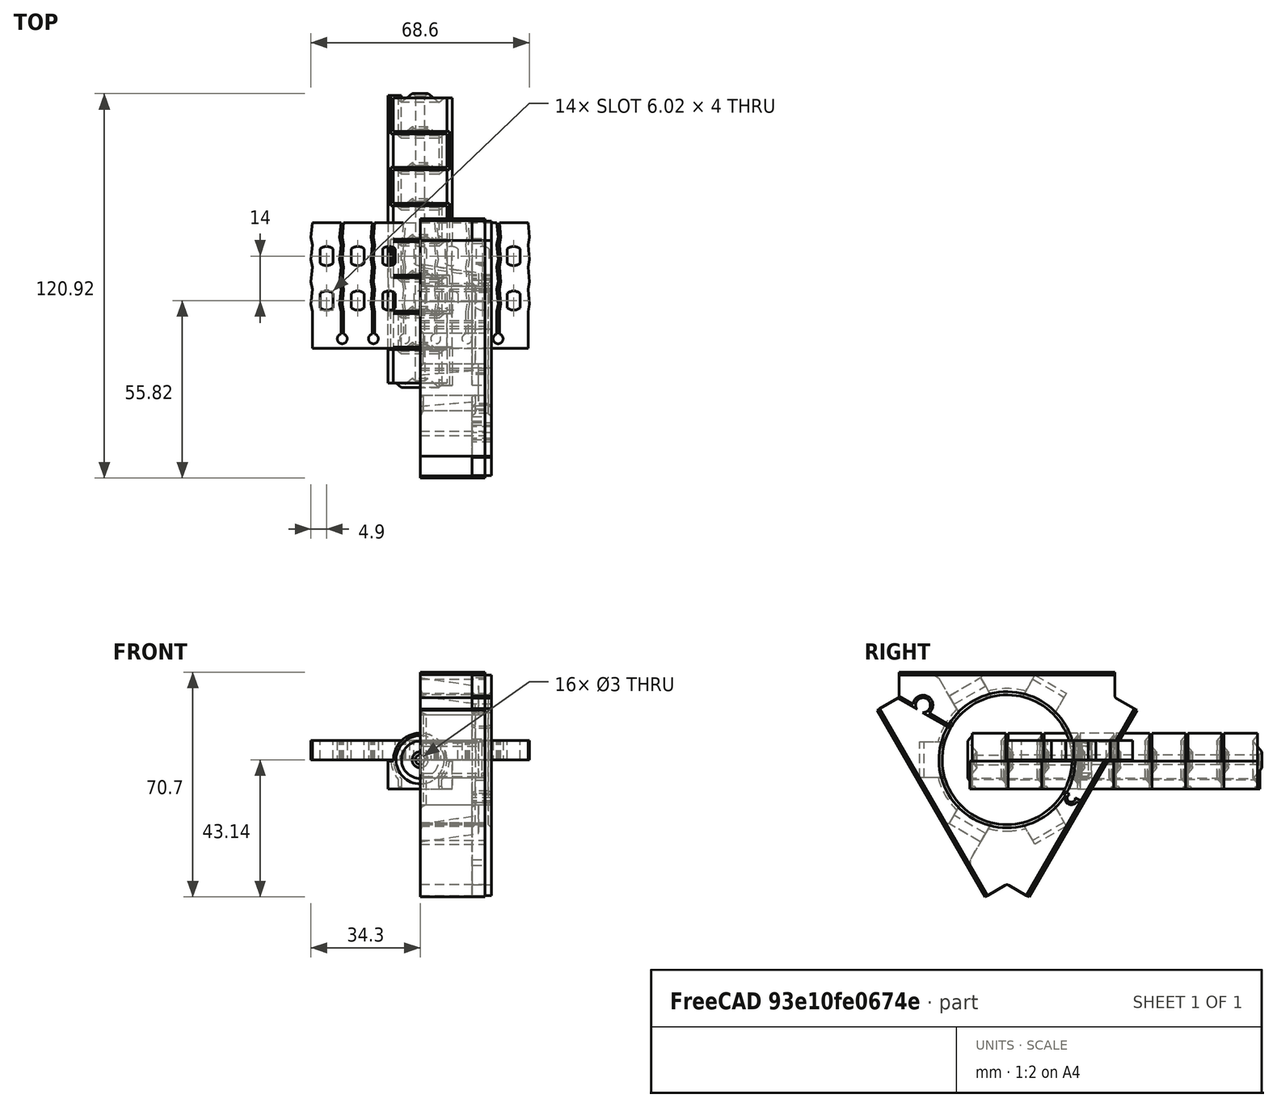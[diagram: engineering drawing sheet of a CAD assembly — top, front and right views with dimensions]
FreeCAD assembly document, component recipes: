
FREECAD ASSEMBLY — COMPONENT RECIPES ("BaseHingeModel_ver1.2_Transmission")

This assembly document has 7 components, labeled P0..P6 below (a component is one placed body or linked part). 6 of them carry a construction recipe — the FreeCAD feature program that regenerates the part from scratch, quoted from this document or its linked companion documents; the rest are supplied as boundary geometry only. No exploded tour is included for this assembly.
COMPONENT P0 — geometry summary ("Assembly"; no construction recipe available for this part):
  bounding box: 182.8 x 158.8 x 20.4 mm
  tessellated surface: 20,696 triangles
  volume: 9578097130411803656351970426578674498653964242418576373807381627235447409514995756881183408189511817567906541525464308833607482709359269325981809199022080 mm^3 (1616738801575943140395693637715189882977871249383409942478852649766611869419882643060896964713126329768861879254438412431142423713072396559864123359232% of its bounding box)
COMPONENT P1 — recipe-attached ("BeamFixatoPart", modeled in this document).
Construction recipe (the document's own serialized feature program — sketch geometry with constraints, then the solid features built on it; lengths are millimeters unless a unit is written):

FEATURE [Sketcher::SketchObject] Sketch022  label="FixatorBodySketch"
  FullyConstrained = false
  MapMode = 5
  Support = -> [XY_Plane005]
  expr: Constraints[143] = Spreadsheet.mmCellWall
  expr: Constraints[144] = Spreadsheet.mmCellWall
  expr: Constraints[145] = Spreadsheet.mmCellWall
  expr: Constraints[146] = Spreadsheet.mmCellWidth
  expr: Constraints[147] = Spreadsheet.mmCellWidth
  expr: Constraints[148] = Spreadsheet.mmCellWidth
  expr: Constraints[169] = Spreadsheet.mmCommonBaseLenght
  expr: Constraints[170] = Spreadsheet.mmToothStep
  expr: Constraints[171] = Spreadsheet.mmToothStep
  expr: Constraints[172] = Spreadsheet.mmToothStep
  expr: Constraints[173] = Spreadsheet.mmToothStep
  expr: Constraints[174] = Spreadsheet.mmToothStep
  expr: Constraints[183] = Spreadsheet.mmCellWall * 3
  expr: Constraints[184] = Spreadsheet.mmCellWall * 3
  expr: Constraints[185] = Spreadsheet.mmCellWall * 3
  expr: Constraints[186] = Spreadsheet.mmCellWall * 3
  expr: Constraints[425] = Spreadsheet.mmFirstCircleArcToBase
  expr: Constraints[435] = Spreadsheet.mmCellWall / 2
  expr: Constraints[464] = Spreadsheet.mmCellWidth + Spreadsheet.mmCellWall
  expr: Constraints[5] = Spreadsheet.mmBaseWidth
  expr: Constraints[6] = Spreadsheet.mmBaseEnd
  sketch-geometry (155):
    g0: LineSegment StartX=-33.9 StartY=0 StartZ=0 EndX=-33.9 EndY=39.5 EndZ=0
    g1: LineSegment StartX=-33.9 StartY=39.5 StartZ=0 EndX=33.9 EndY=39.5 EndZ=0
    g2: LineSegment StartX=33.9 StartY=39.5 StartZ=0 EndX=33.9 EndY=0 EndZ=0
    g3: LineSegment StartX=-73.1099 StartY=25.5 StartZ=0 EndX=65.6354 EndY=25.5 EndZ=0
    g4: LineSegment StartX=-33.9 StartY=0 StartZ=0 EndX=-33.9 EndY=11.5 EndZ=0
    g5: LineSegment StartX=-33.9 StartY=11.5 StartZ=0 EndX=-34.3 EndY=13.9 EndZ=0
    g6: LineSegment StartX=-34.3 StartY=13.9 StartZ=0 EndX=-33.9 EndY=18.5 EndZ=0
    g7: LineSegment StartX=-33.9 StartY=18.5 StartZ=0 EndX=-34.3 EndY=20.9 EndZ=0
    g8: LineSegment StartX=-34.3 StartY=20.9 StartZ=0 EndX=-33.9 EndY=25.5 EndZ=0
    g9: LineSegment StartX=-33.9 StartY=25.5 StartZ=0 EndX=-34.3 EndY=27.9 EndZ=0
    g10: LineSegment StartX=-34.3 StartY=27.9 StartZ=0 EndX=-33.9 EndY=32.5 EndZ=0
    g11: LineSegment StartX=-33.9 StartY=32.5 StartZ=0 EndX=-34.3 EndY=34.9 EndZ=0
    g12: LineSegment StartX=-34.3 StartY=34.9 StartZ=0 EndX=-33.9 EndY=39.5 EndZ=0
    g13: LineSegment StartX=-33.9 StartY=39.5 StartZ=0 EndX=-24.9 EndY=39.5 EndZ=0
    g14: LineSegment StartX=-24.9 StartY=39.5 StartZ=0 EndX=-25.3 EndY=34.9 EndZ=0
    g15: LineSegment StartX=-25.3 StartY=34.9 StartZ=0 EndX=-24.9 EndY=32.5 EndZ=0
    g16: LineSegment StartX=-24.9 StartY=32.5 StartZ=0 EndX=-25.3 EndY=27.9 EndZ=0
    g17: LineSegment StartX=-25.3 StartY=27.9 StartZ=0 EndX=-24.9 EndY=25.5 EndZ=0
    g18: LineSegment StartX=-24.9 StartY=25.5 StartZ=0 EndX=-25.3 EndY=20.9 EndZ=0
    g19: LineSegment StartX=-25.3 StartY=20.9 StartZ=0 EndX=-24.9 EndY=18.5 EndZ=0
    g20: LineSegment StartX=-24.9 StartY=18.5 StartZ=0 EndX=-25.3 EndY=13.9 EndZ=0
    g21: LineSegment StartX=-25.3 StartY=13.9 StartZ=0 EndX=-24.9 EndY=11.5 EndZ=0
    g22: LineSegment StartX=-24.9 StartY=11.5 StartZ=0 EndX=-24.9 EndY=4.5 EndZ=0
    g23: LineSegment StartX=-24.1 StartY=4.5 StartZ=0 EndX=-24.1 EndY=11.5 EndZ=0
    g24: LineSegment StartX=-24.1 StartY=11.5 StartZ=0 EndX=-24.5 EndY=13.9 EndZ=0
    g25: LineSegment StartX=-24.5 StartY=13.9 StartZ=0 EndX=-24.1 EndY=18.5 EndZ=0
    g26: LineSegment StartX=-24.1 StartY=18.5 StartZ=0 EndX=-24.5 EndY=20.9 EndZ=0
    g27: LineSegment StartX=-24.5 StartY=20.9 StartZ=0 EndX=-24.1 EndY=25.5 EndZ=0
    g28: LineSegment StartX=-24.1 StartY=25.5 StartZ=0 EndX=-24.5 EndY=27.9 EndZ=0
    g29: LineSegment StartX=-24.5 StartY=27.9 StartZ=0 EndX=-24.1 EndY=32.5 EndZ=0
    g30: LineSegment StartX=-24.1 StartY=32.5 StartZ=0 EndX=-24.5 EndY=34.9 EndZ=0
    g31: LineSegment StartX=-24.5 StartY=34.9 StartZ=0 EndX=-24.1 EndY=39.5 EndZ=0
    g32: LineSegment StartX=-24.1 StartY=39.5 StartZ=0 EndX=-15.1 EndY=39.5 EndZ=0
    g33: LineSegment StartX=-15.1 StartY=39.5 StartZ=0 EndX=-15.5 EndY=34.9 EndZ=0
    g34: LineSegment StartX=-15.5 StartY=34.9 StartZ=0 EndX=-15.1 EndY=32.5 EndZ=0
    g35: LineSegment StartX=-15.1 StartY=32.5 StartZ=0 EndX=-15.5 EndY=27.9 EndZ=0
    g36: LineSegment StartX=-15.5 StartY=27.9 StartZ=0 EndX=-15.1 EndY=25.5 EndZ=0
    g37: LineSegment StartX=-15.1 StartY=25.5 StartZ=0 EndX=-15.5 EndY=20.9 EndZ=0
    g38: LineSegment StartX=-15.5 StartY=20.9 StartZ=0 EndX=-15.1 EndY=18.5 EndZ=0
    g39: LineSegment StartX=-15.1 StartY=18.5 StartZ=0 EndX=-15.5 EndY=13.9 EndZ=0
    g40: LineSegment StartX=-15.5 StartY=13.9 StartZ=0 EndX=-15.1 EndY=11.5 EndZ=0
    g41: LineSegment StartX=-15.1 StartY=11.5 StartZ=0 EndX=-15.1 EndY=4.5 EndZ=0
    g42: LineSegment StartX=-14.3 StartY=4.5 StartZ=0 EndX=-14.3 EndY=11.5 EndZ=0
    g43: LineSegment StartX=-14.3 StartY=11.5 StartZ=0 EndX=-14.7 EndY=13.9 EndZ=0
    g44: LineSegment StartX=-14.7 StartY=13.9 StartZ=0 EndX=-14.3 EndY=18.5 EndZ=0
    g45: LineSegment StartX=-14.3 StartY=18.5 StartZ=0 EndX=-14.7 EndY=20.9 EndZ=0
    g46: LineSegment StartX=-14.7 StartY=20.9 StartZ=0 EndX=-14.3 EndY=25.5 EndZ=0
    g47: LineSegment StartX=-14.3 StartY=25.5 StartZ=0 EndX=-14.7 EndY=27.9 EndZ=0
    g48: LineSegment StartX=-14.7 StartY=27.9 StartZ=0 EndX=-14.3 EndY=32.5 EndZ=0
    g49: LineSegment StartX=-14.3 StartY=32.5 StartZ=0 EndX=-14.7 EndY=34.9 EndZ=0
    g50: LineSegment StartX=-14.7 StartY=34.9 StartZ=0 EndX=-14.3 EndY=39.5 EndZ=0
    g51: LineSegment StartX=-14.3 StartY=39.5 StartZ=0 EndX=-5.3 EndY=39.5 EndZ=0
    g52: LineSegment StartX=-5.3 StartY=39.5 StartZ=0 EndX=-5.7 EndY=34.9 EndZ=0
    g53: LineSegment StartX=-5.7 StartY=34.9 StartZ=0 EndX=-5.3 EndY=32.5 EndZ=0
    g54: LineSegment StartX=-5.3 StartY=32.5 StartZ=0 EndX=-5.7 EndY=27.9 EndZ=0
    g55: LineSegment StartX=-5.7 StartY=27.9 StartZ=0 EndX=-5.3 EndY=25.5 EndZ=0
    g56: LineSegment StartX=-5.3 StartY=25.5 StartZ=0 EndX=-5.7 EndY=20.9 EndZ=0
    g57: LineSegment StartX=-5.7 StartY=20.9 StartZ=0 EndX=-5.3 EndY=18.5 EndZ=0
    g58: LineSegment StartX=-5.3 StartY=18.5 StartZ=0 EndX=-5.7 EndY=13.9 EndZ=0
    g59: LineSegment StartX=-5.7 StartY=13.9 StartZ=0 EndX=-5.3 EndY=11.5 EndZ=0
    g60: LineSegment StartX=-5.3 StartY=11.5 StartZ=0 EndX=-5.3 EndY=4.5 EndZ=0
    g61: LineSegment StartX=-4.5 StartY=4.5 StartZ=0 EndX=-4.5 EndY=11.5 EndZ=0
    g62: LineSegment StartX=-4.5 StartY=11.5 StartZ=0 EndX=-4.9 EndY=13.9 EndZ=0
    g63: LineSegment StartX=-4.9 StartY=13.9 StartZ=0 EndX=-4.5 EndY=18.5 EndZ=0
    g64: LineSegment StartX=-4.5 StartY=18.5 StartZ=0 EndX=-4.9 EndY=20.9 EndZ=0
    g65: LineSegment StartX=-4.9 StartY=20.9 StartZ=0 EndX=-4.5 EndY=25.5 EndZ=0
    g66: LineSegment StartX=-4.5 StartY=25.5 StartZ=0 EndX=-4.9 EndY=27.9 EndZ=0
    g67: LineSegment StartX=-4.9 StartY=27.9 StartZ=0 EndX=-4.5 EndY=32.5 EndZ=0
    g68: LineSegment StartX=-4.5 StartY=32.5 StartZ=0 EndX=-4.9 EndY=34.9 EndZ=0
    g69: LineSegment StartX=-4.9 StartY=34.9 StartZ=0 EndX=-4.5 EndY=39.5 EndZ=0
    g70: LineSegment StartX=-4.5 StartY=39.5 StartZ=0 EndX=4.5 EndY=39.5 EndZ=0
    g71: LineSegment StartX=4.5 StartY=39.5 StartZ=0 EndX=4.9 EndY=34.9 EndZ=0
    g72: LineSegment StartX=4.9 StartY=34.9 StartZ=0 EndX=4.5 EndY=32.5 EndZ=0
    g73: LineSegment StartX=4.5 StartY=32.5 StartZ=0 EndX=4.9 EndY=27.9 EndZ=0
    g74: LineSegment StartX=4.9 StartY=27.9 StartZ=0 EndX=4.5 EndY=25.5 EndZ=0
    g75: LineSegment StartX=4.5 StartY=25.5 StartZ=0 EndX=4.9 EndY=20.9 EndZ=0
    g76: LineSegment StartX=4.9 StartY=20.9 StartZ=0 EndX=4.5 EndY=18.5 EndZ=0
    g77: LineSegment StartX=4.5 StartY=18.5 StartZ=0 EndX=4.9 EndY=13.9 EndZ=0
    g78: LineSegment StartX=4.9 StartY=13.9 StartZ=0 EndX=4.5 EndY=11.5 EndZ=0
    g79: LineSegment StartX=4.5 StartY=11.5 StartZ=0 EndX=4.5 EndY=4.5 EndZ=0
    g80: LineSegment StartX=5.3 StartY=4.5 StartZ=0 EndX=5.3 EndY=11.5 EndZ=0
    g81: LineSegment StartX=5.3 StartY=11.5 StartZ=0 EndX=5.7 EndY=13.9 EndZ=0
    g82: LineSegment StartX=5.7 StartY=13.9 StartZ=0 EndX=5.3 EndY=18.5 EndZ=0
    g83: LineSegment StartX=5.3 StartY=18.5 StartZ=0 EndX=5.7 EndY=20.9 EndZ=0
    g84: LineSegment StartX=5.7 StartY=20.9 StartZ=0 EndX=5.3 EndY=25.5 EndZ=0
    g85: LineSegment StartX=5.3 StartY=25.5 StartZ=0 EndX=5.7 EndY=27.9 EndZ=0
    g86: LineSegment StartX=5.7 StartY=27.9 StartZ=0 EndX=5.3 EndY=32.5 EndZ=0
    g87: LineSegment StartX=5.3 StartY=32.5 StartZ=0 EndX=5.7 EndY=34.9 EndZ=0
    g88: LineSegment StartX=5.7 StartY=34.9 StartZ=0 EndX=5.3 EndY=39.5 EndZ=0
    g89: LineSegment StartX=5.3 StartY=39.5 StartZ=0 EndX=14.3 EndY=39.5 EndZ=0
    g90: LineSegment StartX=14.3 StartY=39.5 StartZ=0 EndX=14.7 EndY=34.9 EndZ=0
    g91: LineSegment StartX=14.7 StartY=34.9 StartZ=0 EndX=14.3 EndY=32.5 EndZ=0
    g92: LineSegment StartX=14.3 StartY=32.5 StartZ=0 EndX=14.7 EndY=27.9 EndZ=0
    g93: LineSegment StartX=14.7 StartY=27.9 StartZ=0 EndX=14.3 EndY=25.5 EndZ=0
    g94: LineSegment StartX=14.3 StartY=25.5 StartZ=0 EndX=14.7 EndY=20.9 EndZ=0
    g95: LineSegment StartX=14.7 StartY=20.9 StartZ=0 EndX=14.3 EndY=18.5 EndZ=0
    g96: LineSegment StartX=14.3 StartY=18.5 StartZ=0 EndX=14.7 EndY=13.9 EndZ=0
    g97: LineSegment StartX=14.7 StartY=13.9 StartZ=0 EndX=14.3 EndY=11.5 EndZ=0
    g98: LineSegment StartX=14.3 StartY=11.5 StartZ=0 EndX=14.3 EndY=4.5 EndZ=0
    g99: LineSegment StartX=15.1 StartY=4.5 StartZ=0 EndX=15.1 EndY=11.5 EndZ=0
    g100: LineSegment StartX=15.1 StartY=11.5 StartZ=0 EndX=15.5 EndY=13.9 EndZ=0
    g101: LineSegment StartX=15.5 StartY=13.9 StartZ=0 EndX=15.1 EndY=18.5 EndZ=0
    g102: LineSegment StartX=15.1 StartY=18.5 StartZ=0 EndX=15.5 EndY=20.9 EndZ=0
    g103: LineSegment StartX=15.5 StartY=20.9 StartZ=0 EndX=15.1 EndY=25.5 EndZ=0
    g104: LineSegment StartX=15.1 StartY=25.5 StartZ=0 EndX=15.5 EndY=27.9 EndZ=0
    g105: LineSegment StartX=15.5 StartY=27.9 StartZ=0 EndX=15.1 EndY=32.5 EndZ=0
    g106: LineSegment StartX=15.1 StartY=32.5 StartZ=0 EndX=15.5 EndY=34.9 EndZ=0
    g107: LineSegment StartX=15.5 StartY=34.9 StartZ=0 EndX=15.1 EndY=39.5 EndZ=0
    g108: LineSegment StartX=15.1 StartY=39.5 StartZ=0 EndX=24.1 EndY=39.5 EndZ=0
    g109: LineSegment StartX=24.1 StartY=39.5 StartZ=0 EndX=24.5 EndY=34.9 EndZ=0
    g110: LineSegment StartX=24.5 StartY=34.9 StartZ=0 EndX=24.1 EndY=32.5 EndZ=0
    g111: LineSegment StartX=24.1 StartY=32.5 StartZ=0 EndX=24.5 EndY=27.9 EndZ=0
    g112: LineSegment StartX=24.5 StartY=27.9 StartZ=0 EndX=24.1 EndY=25.5 EndZ=0
    g113: LineSegment StartX=24.1 StartY=25.5 StartZ=0 EndX=24.5 EndY=20.9 EndZ=0
    g114: LineSegment StartX=24.5 StartY=20.9 StartZ=0 EndX=24.1 EndY=18.5 EndZ=0
    g115: LineSegment StartX=24.1 StartY=18.5 StartZ=0 EndX=24.5 EndY=13.9 EndZ=0
    g116: LineSegment StartX=24.5 StartY=13.9 StartZ=0 EndX=24.1 EndY=11.5 EndZ=0
    g117: LineSegment StartX=24.1 StartY=11.5 StartZ=0 EndX=24.1 EndY=4.5 EndZ=0
    g118: LineSegment StartX=24.9 StartY=4.5 StartZ=0 EndX=24.9 EndY=11.5 EndZ=0
    g119: LineSegment StartX=24.9 StartY=11.5 StartZ=0 EndX=25.3 EndY=13.9 EndZ=0
    g120: LineSegment StartX=25.3 StartY=13.9 StartZ=0 EndX=24.9 EndY=18.5 EndZ=0
    g121: LineSegment StartX=24.9 StartY=18.5 StartZ=0 EndX=25.3 EndY=20.9 EndZ=0
    g122: LineSegment StartX=25.3 StartY=20.9 StartZ=0 EndX=24.9 EndY=25.5 EndZ=0
    g123: LineSegment StartX=24.9 StartY=25.5 StartZ=0 EndX=25.3 EndY=27.9 EndZ=0
    g124: LineSegment StartX=25.3 StartY=27.9 StartZ=0 EndX=24.9 EndY=32.5 EndZ=0
    g125: LineSegment StartX=24.9 StartY=32.5 StartZ=0 EndX=25.3 EndY=34.9 EndZ=0
    g126: LineSegment StartX=25.3 StartY=34.9 StartZ=0 EndX=24.9 EndY=39.5 EndZ=0
    g127: LineSegment StartX=24.9 StartY=39.5 StartZ=0 EndX=33.9 EndY=39.5 EndZ=0
    g128: LineSegment StartX=33.9 StartY=39.5 StartZ=0 EndX=34.3 EndY=34.9 EndZ=0
    g129: LineSegment StartX=34.3 StartY=34.9 StartZ=0 EndX=33.9 EndY=32.5 EndZ=0
    g130: LineSegment StartX=33.9 StartY=32.5 StartZ=0 EndX=34.3 EndY=27.9 EndZ=0
    g131: LineSegment StartX=34.3 StartY=27.9 StartZ=0 EndX=33.9 EndY=25.5 EndZ=0
    g132: LineSegment StartX=33.9 StartY=25.5 StartZ=0 EndX=34.3 EndY=20.9 EndZ=0
    g133: LineSegment StartX=34.3 StartY=20.9 StartZ=0 EndX=33.9 EndY=18.5 EndZ=0
    g134: LineSegment StartX=33.9 StartY=18.5 StartZ=0 EndX=34.3 EndY=13.9 EndZ=0
    g135: LineSegment StartX=34.3 StartY=13.9 StartZ=0 EndX=33.9 EndY=11.5 EndZ=0
    g136: LineSegment StartX=33.9 StartY=11.5 StartZ=0 EndX=33.9 EndY=0 EndZ=0
    g137: LineSegment StartX=33.9 StartY=0 StartZ=0 EndX=-33.9 EndY=0 EndZ=0
    g138: LineSegment StartX=-73.1099 StartY=18.5 StartZ=0 EndX=65.6354 EndY=18.5 EndZ=0
    g139: LineSegment StartX=-73.1099 StartY=34.9 StartZ=0 EndX=65.6354 EndY=34.9 EndZ=0
    g140: LineSegment StartX=-73.1099 StartY=32.5 StartZ=0 EndX=65.6354 EndY=32.5 EndZ=0
    g141: LineSegment StartX=-73.1099 StartY=27.9 StartZ=0 EndX=65.6354 EndY=27.9 EndZ=0
    g142: LineSegment StartX=-73.1099 StartY=20.9 StartZ=0 EndX=65.6354 EndY=20.9 EndZ=0
    g143: LineSegment StartX=-73.1099 StartY=11.5 StartZ=0 EndX=65.6354 EndY=11.5 EndZ=0
    g144: LineSegment StartX=-34.3 StartY=8.59208 StartZ=0 EndX=-34.3 EndY=49.4346 EndZ=0
    g145: LineSegment StartX=-73.1099 StartY=13.9 StartZ=0 EndX=65.6354 EndY=13.9 EndZ=0
    g146: LineSegment StartX=-33.9 StartY=0 StartZ=0 EndX=33.9 EndY=0 EndZ=0
    g147: LineSegment StartX=-73.1099 StartY=4.5 StartZ=0 EndX=65.6354 EndY=4.5 EndZ=0
    g148: ArcOfCircle CenterX=-24.5 CenterY=3 CenterZ=0 NormalX=0 NormalY=0 NormalZ=1 AngleXU=0 Radius=1.55242 StartAngle=1.8314 EndAngle=7.59338
    g149: ArcOfCircle CenterX=-14.7 CenterY=3 CenterZ=0 NormalX=0 NormalY=0 NormalZ=1 AngleXU=0 Radius=1.55242 StartAngle=1.8314 EndAngle=7.59338
    g150: ArcOfCircle CenterX=-4.9 CenterY=3 CenterZ=0 NormalX=0 NormalY=0 NormalZ=1 AngleXU=0 Radius=1.55242 StartAngle=1.8314 EndAngle=7.59338
    g151: ArcOfCircle CenterX=4.9 CenterY=3 CenterZ=0 NormalX=0 NormalY=0 NormalZ=1 AngleXU=0 Radius=1.55242 StartAngle=1.8314 EndAngle=7.59338
    g152: ArcOfCircle CenterX=14.7 CenterY=3 CenterZ=0 NormalX=0 NormalY=0 NormalZ=1 AngleXU=0 Radius=1.55242 StartAngle=1.8314 EndAngle=7.59338
    g153: ArcOfCircle CenterX=24.5 CenterY=3 CenterZ=0 NormalX=0 NormalY=0 NormalZ=1 AngleXU=0 Radius=1.55242 StartAngle=1.8314 EndAngle=7.59338
    g154: LineSegment StartX=-73.1099 StartY=3 StartZ=0 EndX=65.6354 EndY=3 EndZ=0
  constraints (469):
    c: Coincident(g0,g1)
    c: Coincident(g1,g2)
    c: Horizontal(g3)
    c: Symmetric(g0,g2,g-2)
    c: Symmetric(g1,g0,g-2)
    c: DistanceX(g0,g2) = 67.8
    c: DistanceX(g0,g1) = 67.8
    c: Coincident(g4,g5)
    c: Coincident(g5,g6)
    c: Coincident(g6,g7)
    c: Coincident(g7,g8)
    c: Coincident(g8,g9)
    c: Coincident(g9,g10)
    c: Coincident(g10,g11)
    c: Coincident(g11,g12)
    c: Coincident(g12,g13)
    c: Horizontal(g13)
    c: Coincident(g13,g14)
    c: Coincident(g14,g15)
    c: Coincident(g15,g16)
    c: Coincident(g16,g17)
    c: Coincident(g17,g18)
    c: Coincident(g18,g19)
    c: Coincident(g19,g20)
    c: Coincident(g20,g21)
    c: Coincident(g21,g22)
    c: Coincident(g23,g24)
    c: Coincident(g24,g25)
    c: Coincident(g25,g26)
    c: Coincident(g26,g27)
    c: Coincident(g27,g28)
    c: Coincident(g28,g29)
    c: Coincident(g29,g30)
    c: Coincident(g30,g31)
    c: Coincident(g31,g32)
    c: Horizontal(g32)
    c: Coincident(g32,g33)
    c: Coincident(g33,g34)
    c: Coincident(g34,g35)
    c: Coincident(g35,g36)
    c: Coincident(g36,g37)
    c: Coincident(g37,g38)
    c: Coincident(g38,g39)
    c: Coincident(g39,g40)
    c: Coincident(g40,g41)
    c: Coincident(g42,g43)
    c: Coincident(g43,g44)
    c: Coincident(g44,g45)
    c: Coincident(g45,g46)
    c: Coincident(g46,g47)
    c: Coincident(g47,g48)
    c: Coincident(g48,g49)
    c: Coincident(g49,g50)
    c: Coincident(g50,g51)
    c: Coincident(g51,g52)
    c: Coincident(g52,g53)
    c: Coincident(g53,g54)
    c: Coincident(g54,g55)
    c: Coincident(g55,g56)
    c: Coincident(g56,g57)
    c: Coincident(g57,g58)
    c: Coincident(g58,g59)
    c: Coincident(g59,g60)
    c: Coincident(g61,g62)
    c: Coincident(g62,g63)
    c: Coincident(g63,g64)
    c: Coincident(g64,g65)
    c: Coincident(g65,g66)
    c: Coincident(g66,g67)
    c: Coincident(g67,g68)
    c: Coincident(g68,g69)
    c: Coincident(g69,g70)
    c: Coincident(g70,g71)
    c: Coincident(g71,g72)
    c: Coincident(g72,g73)
    c: Coincident(g73,g74)
    c: Coincident(g74,g75)
    c: Coincident(g75,g76)
    c: Coincident(g76,g77)
    c: Coincident(g77,g78)
    c: Coincident(g78,g79)
    c: Coincident(g80,g81)
    c: Coincident(g81,g82)
    c: Coincident(g82,g83)
    c: Coincident(g83,g84)
    c: Coincident(g84,g85)
    c: Coincident(g85,g86)
    c: Coincident(g86,g87)
    c: Coincident(g87,g88)
    c: Coincident(g88,g89)
    c: Horizontal(g89)
    c: Coincident(g89,g90)
    c: Coincident(g90,g91)
    c: Coincident(g91,g92)
    c: Coincident(g92,g93)
    c: Coincident(g93,g94)
    c: Coincident(g94,g95)
    c: Coincident(g95,g96)
    c: Coincident(g96,g97)
    c: Coincident(g97,g98)
    c: Coincident(g99,g100)
    c: Coincident(g100,g101)
    c: Coincident(g101,g102)
    c: Coincident(g102,g103)
    c: Coincident(g103,g104)
    c: Coincident(g104,g105)
    c: Coincident(g105,g106)
    c: Coincident(g106,g107)
    c: Coincident(g107,g108)
    c: Coincident(g108,g109)
    c: Coincident(g109,g110)
    c: Coincident(g110,g111)
    c: Coincident(g111,g112)
    c: Coincident(g112,g113)
    c: Coincident(g113,g114)
    c: Coincident(g114,g115)
    c: Coincident(g115,g116)
    c: Coincident(g116,g117)
    c: Coincident(g118,g119)
    c: Coincident(g119,g120)
    c: Coincident(g120,g121)
    c: Coincident(g121,g122)
    c: Coincident(g122,g123)
    c: Coincident(g123,g124)
    c: Coincident(g124,g125)
    c: Coincident(g125,g126)
    c: Coincident(g126,g127)
    c: Coincident(g127,g128)
    c: Coincident(g128,g129)
    c: Coincident(g129,g130)
    c: Coincident(g130,g131)
    c: Coincident(g131,g132)
    c: Coincident(g132,g133)
    c: Coincident(g133,g134)
    c: Coincident(g134,g135)
    c: Coincident(g135,g136)
    c: Symmetric(g69,g70,g-2)
    c: Symmetric(g51,g88,g-2)
    c: Symmetric(g50,g89,g-2)
    c: Symmetric(g32,g107,g-2)
    c: Symmetric(g31,g108,g-2)
    c: Symmetric(g13,g126,g-2)
    c: Symmetric(g12,g127,g-2)
    c: DistanceX(g13,g31) = 0.8
    c: DistanceX(g32,g50) = 0.8
    c: DistanceX(g51,g69) = 0.8
    c: DistanceX(g13,g13) = 9
    c: DistanceX(g32,g32) = 9
    c: DistanceX(g51,g51) = 9
    c: Horizontal(g139)
    c: Horizontal(g140)
    c: Horizontal(g141)
    c: Horizontal(g142)
    c: Horizontal(g143)
    c: Vertical(g8,g6)
    c: Vertical(g6,g4)
    c: Vertical(g144)
    c: Horizontal(g145)
    c: Coincident(g146,g0)
    c: Coincident(g146,g2)
    c: Coincident(g0,g137)
    c: Coincident(g2,g137)
    c: Horizontal(g147)
    c: PointOnObject(g11,g139)
    c: PointOnObject(g11,g144)
    c: PointOnObject(g10,g140)
    c: PointOnObject(g9,g144)
    c: PointOnObject(g7,g142)
    c: Horizontal(g138)
    c: DistanceY(g137,g147) = 4.5
    c: DistanceY(g147,g143) = 7
    c: DistanceY(g143,g138) = 7
    c: DistanceY(g138,g3) = 7
    c: DistanceY(g3,g140) = 7
    c: DistanceY(g140,g0) = 7
    c: Vertical(g139,g140)
    c: Vertical(g140,g141)
    c: Vertical(g141,g3)
    c: Vertical(g3,g142)
    c: Vertical(g142,g138)
    c: Vertical(g138,g145)
    c: Vertical(g145,g143)
    c: Vertical(g143,g147)
    c: DistanceY(g143,g145) = 2.4
    c: DistanceY(g138,g142) = 2.4
    c: DistanceY(g3,g141) = 2.4
    c: DistanceY(g140,g139) = 2.4
    c: Parallel(g12,g14)
    c: Parallel(g11,g15)
    c: PointOnObject(g14,g139)
    c: PointOnObject(g30,g139)
    c: PointOnObject(g15,g140)
    c: PointOnObject(g29,g140)
    c: Parallel(g14,g31)
    c: PointOnObject(g16,g141)
    c: PointOnObject(g28,g141)
    c: PointOnObject(g17,g3)
    c: PointOnObject(g27,g3)
    c: PointOnObject(g18,g142)
    c: PointOnObject(g26,g142)
    c: PointOnObject(g19,g138)
    c: PointOnObject(g25,g138)
    c: PointOnObject(g20,g145)
    c: PointOnObject(g24,g145)
    c: PointOnObject(g21,g143)
    c: PointOnObject(g23,g143)
    c: PointOnObject(g22,g147)
    c: PointOnObject(g23,g147)
    c: PointOnObject(g33,g139)
    c: PointOnObject(g49,g139)
    c: PointOnObject(g52,g139)
    c: PointOnObject(g71,g139)
    c: PointOnObject(g87,g139)
    c: PointOnObject(g90,g139)
    c: PointOnObject(g106,g139)
    c: PointOnObject(g109,g139)
    c: PointOnObject(g125,g139)
    c: PointOnObject(g128,g139)
    c: PointOnObject(g34,g140)
    c: PointOnObject(g48,g140)
    c: PointOnObject(g53,g140)
    c: PointOnObject(g67,g140)
    c: PointOnObject(g72,g140)
    c: PointOnObject(g86,g140)
    c: PointOnObject(g91,g140)
    c: PointOnObject(g105,g140)
    c: PointOnObject(g110,g140)
    c: PointOnObject(g124,g140)
    c: PointOnObject(g129,g140)
    c: Parallel(g33,g50)
    c: Parallel(g52,g69)
    c: Parallel(g71,g88)
    c: Parallel(g71,g90)
    c: Parallel(g90,g107)
    c: Parallel(g71,g109)
    c: Parallel(g109,g126)
    c: Parallel(g126,g128)
    c: Symmetric(g71,g68,g-2)
    c: Symmetric(g72,g67,g-2)
    c: Vertical(g139,g140)
    c: Vertical(g140,g141)
    c: Vertical(g141,g3)
    c: Vertical(g3,g142)
    c: Vertical(g142,g138)
    c: Vertical(g138,g145)
    c: Vertical(g145,g143)
    c: Vertical(g143,g147)
    c: Parallel(g34,g49)
    c: Parallel(g49,g53)
    c: Parallel(g53,g68)
    c: Parallel(g35,g48)
    c: Parallel(g48,g54)
    c: Parallel(g54,g67)
    c: PointOnObject(g35,g141)
    c: PointOnObject(g47,g141)
    c: PointOnObject(g54,g141)
    c: PointOnObject(g66,g141)
    c: PointOnObject(g85,g141)
    c: PointOnObject(g92,g141)
    c: PointOnObject(g104,g141)
    c: PointOnObject(g111,g141)
    c: PointOnObject(g123,g141)
    c: PointOnObject(g130,g141)
    c: Symmetric(g66,g73,g-2)
    c: Symmetric(g65,g74,g-2)
    c: PointOnObject(g36,g3)
    c: PointOnObject(g46,g3)
    c: PointOnObject(g55,g3)
    c: PointOnObject(g65,g3)
    c: Parallel(g36,g47)
    c: Parallel(g47,g55)
    c: Parallel(g55,g66)
    c: Symmetric(g64,g75,g-2)
    c: Symmetric(g79,g61,g-2)
    c: Symmetric(g61,g78,g-2)
    c: Symmetric(g62,g77,g-2)
    c: Symmetric(g63,g76,g-2)
    c: Parallel(g37,g46)
    c: Parallel(g46,g56)
    c: Parallel(g56,g65)
    c: PointOnObject(g37,g142)
    c: PointOnObject(g45,g142)
    c: PointOnObject(g56,g142)
    c: PointOnObject(g64,g142)
    c: PointOnObject(g38,g138)
    c: PointOnObject(g44,g138)
    c: PointOnObject(g57,g138)
    c: PointOnObject(g63,g138)
    c: Parallel(g38,g45)
    c: Parallel(g45,g57)
    c: Parallel(g57,g64)
    c: PointOnObject(g39,g145)
    c: PointOnObject(g43,g145)
    c: PointOnObject(g58,g145)
    c: PointOnObject(g62,g145)
    c: Parallel(g39,g44)
    c: Parallel(g44,g58)
    c: Parallel(g58,g63)
    c: Parallel(g40,g43)
    c: Parallel(g43,g59)
    c: Parallel(g59,g62)
    c: PointOnObject(g40,g143)
    c: PointOnObject(g42,g143)
    c: PointOnObject(g59,g143)
    c: PointOnObject(g61,g143)
    c: PointOnObject(g41,g147)
    c: PointOnObject(g42,g147)
    c: PointOnObject(g60,g147)
    c: PointOnObject(g61,g147)
    c: Parallel(g41,g42)
    c: Parallel(g42,g60)
    c: Parallel(g60,g61)
    c: PointOnObject(g80,g147)
    c: PointOnObject(g98,g147)
    c: PointOnObject(g99,g147)
    c: PointOnObject(g117,g147)
    c: PointOnObject(g118,g147)
    c: PointOnObject(g80,g143)
    c: PointOnObject(g97,g143)
    c: PointOnObject(g99,g143)
    c: PointOnObject(g116,g143)
    c: PointOnObject(g118,g143)
    c: PointOnObject(g135,g143)
    c: Parallel(g79,g80)
    c: Parallel(g80,g98)
    c: Parallel(g98,g99)
    c: Parallel(g99,g117)
    c: Parallel(g117,g118)
    c: Parallel(g118,g136)
    c: Parallel(g72,g87)
    c: Parallel(g87,g91)
    c: Parallel(g91,g106)
    c: Parallel(g106,g110)
    c: Parallel(g110,g125)
    c: Parallel(g125,g129)
    c: Parallel(g73,g86)
    c: Parallel(g86,g92)
    c: Parallel(g92,g105)
    c: Parallel(g105,g111)
    c: Parallel(g111,g124)
    c: Parallel(g124,g130)
    c: PointOnObject(g84,g3)
    c: PointOnObject(g93,g3)
    c: PointOnObject(g103,g3)
    c: PointOnObject(g112,g3)
    c: PointOnObject(g122,g3)
    c: PointOnObject(g131,g3)
    c: Parallel(g74,g85)
    c: Parallel(g85,g93)
    c: Parallel(g93,g104)
    c: Parallel(g104,g112)
    c: Parallel(g112,g123)
    c: Parallel(g123,g131)
    c: PointOnObject(g83,g142)
    c: PointOnObject(g94,g142)
    c: PointOnObject(g102,g142)
    c: PointOnObject(g113,g142)
    c: PointOnObject(g121,g142)
    c: PointOnObject(g132,g142)
    c: Parallel(g75,g84)
    c: Parallel(g84,g94)
    c: Parallel(g94,g103)
    c: Parallel(g103,g113)
    c: Parallel(g113,g122)
    c: Parallel(g122,g132)
    c: PointOnObject(g82,g138)
    c: PointOnObject(g95,g138)
    c: PointOnObject(g101,g138)
    c: PointOnObject(g114,g138)
    c: PointOnObject(g120,g138)
    c: PointOnObject(g133,g138)
    c: PointOnObject(g81,g145)
    c: PointOnObject(g96,g145)
    c: PointOnObject(g100,g145)
    c: PointOnObject(g115,g145)
    c: PointOnObject(g119,g145)
    c: PointOnObject(g134,g145)
    c: Parallel(g76,g83)
    c: Parallel(g83,g95)
    c: Parallel(g95,g102)
    c: Parallel(g102,g114)
    c: Parallel(g114,g121)
    c: Parallel(g121,g133)
    c: Parallel(g77,g82)
    c: Parallel(g82,g96)
    c: Parallel(g96,g101)
    c: Parallel(g101,g115)
    c: Parallel(g115,g120)
    c: Parallel(g120,g134)
    c: Parallel(g78,g81)
    c: Parallel(g81,g97)
    c: Parallel(g97,g100)
    c: Parallel(g100,g116)
    c: Parallel(g116,g119)
    c: Parallel(g119,g135)
    c: DistanceY(g137,g-1) = 0
    c: PointOnObject(g148,g154)
    c: PointOnObject(g149,g154)
    c: PointOnObject(g150,g154)
    c: PointOnObject(g151,g154)
    c: PointOnObject(g152,g154)
    c: PointOnObject(g153,g154)
    c: PointOnObject(g22,g148)
    c: PointOnObject(g23,g148)
    c: PointOnObject(g41,g149)
    c: PointOnObject(g42,g149)
    c: PointOnObject(g60,g150)
    c: PointOnObject(g61,g150)
    c: PointOnObject(g79,g151)
    c: PointOnObject(g98,g152)
    c: PointOnObject(g99,g152)
    c: PointOnObject(g117,g153)
    c: PointOnObject(g118,g153)
    c: PointOnObject(g153,g147)
    c: PointOnObject(g153,g147)
    c: PointOnObject(g152,g147)
    c: PointOnObject(g152,g147)
    c: PointOnObject(g151,g147)
    c: PointOnObject(g151,g147)
    c: PointOnObject(g150,g147)
    c: PointOnObject(g150,g147)
    c: PointOnObject(g149,g147)
    c: PointOnObject(g149,g147)
    c: PointOnObject(g148,g147)
    c: PointOnObject(g148,g147)
    c: DistanceY(g154,g147) = 1.5
    c: Vertical(g147,g154)
    c: Vertical(g147,g154)
    c: Coincident(g136,g137)
    c: Coincident(g4,g137)
    c: Coincident(g0,g12)
    c: PointOnObject(g31,g1)
    c: PointOnObject(g50,g1)
    c: PointOnObject(g69,g1)
    c: PointOnObject(g6,g0)
    c: DistanceX(g144,g12) = 0.4
    c: PointOnObject(g9,g141)
    c: PointOnObject(g8,g3)
    c: PointOnObject(g7,g144)
    c: PointOnObject(g6,g138)
    c: PointOnObject(g5,g145)
    c: PointOnObject(g5,g144)
    c: PointOnObject(g4,g143)
    c: Parallel(g12,g33)
    c: Parallel(g12,g52)
    c: Parallel(g15,g30)
    c: Parallel(g11,g34)
    c: PointOnObject(g10,g0)
    c: Parallel(g16,g29)
    c: Parallel(g10,g16)
    c: Parallel(g10,g35)
    c: Parallel(g9,g17)
    c: Parallel(g17,g28)
    c: Parallel(g9,g36)
    c: Parallel(g18,g27)
    c: Parallel(g8,g18)
    c: Parallel(g8,g37)
    c: Parallel(g7,g19)
    c: Parallel(g19,g26)
    c: Parallel(g6,g20)
    c: Parallel(g20,g25)
    c: Parallel(g7,g38)
    c: Parallel(g6,g39)
    c: Symmetric(g150,g151,g-2)
    c: DistanceX(g150,g151) = 9.8
    c: Parallel(g23,g22)
    c: Parallel(g21,g24)
    c: Parallel(g5,g21)
    c: Parallel(g41,g23)
FEATURE [PartDesign::Pad] Pad  label="FixatorPadBody"
  Direction = (0,0,1)
  Length = 6
  Length2 = 10
  Profile = -> Sketch022
  ReferenceAxis = -> Sketch022 [N_Axis]
  Type = 0
  expr: Length = Spreadsheet.mmCellHight
FEATURE [Sketcher::SketchObject] Sketch  label="PiercesPocketSketch"
  AttachmentOffset = pos=(0,0,0) rot=(1,0,0;1.5708rad)
  FullyConstrained = true
  MapMode = 2
  Placement = pos=(0,0,0) rot=(0.707107,0.707107,0;3.14159rad)
  Support = -> [YZ_Plane005]
  expr: Constraints[108] = Spreadsheet.mmCellPierceWidth
  expr: Constraints[118] = Spreadsheet.mmCellPierceWidth
  expr: Constraints[128] = Spreadsheet.mmCellPierceWidth
  expr: Constraints[138] = Spreadsheet.mmCellPierceWidth
  expr: Constraints[148] = Spreadsheet.mmCellPierceWidth
  expr: Constraints[158] = Spreadsheet.mmCellPierceWidth
  expr: Constraints[171] = Spreadsheet.mmCellWidth + Spreadsheet.mmCellWall
  expr: Constraints[172] = Spreadsheet.mmCellWidth + Spreadsheet.mmCellWall
  expr: Constraints[173] = Spreadsheet.mmCellWidth + Spreadsheet.mmCellWall
  expr: Constraints[174] = Spreadsheet.mmCellWidth + Spreadsheet.mmCellWall
  expr: Constraints[175] = Spreadsheet.mmCellWidth + Spreadsheet.mmCellWall
  expr: Constraints[176] = Spreadsheet.mmCellWidth + Spreadsheet.mmCellWall
  expr: Constraints[178] = Spreadsheet.mmCellWidth / 2
  expr: Constraints[179] = Spreadsheet.mmCellWidth / 2
  expr: Constraints[180] = Spreadsheet.mmCommonBaseLenght + Spreadsheet.mmToothStep * 1.5
  expr: Constraints[181] = Spreadsheet.mmToothStep * 2
  expr: Constraints[19] = Spreadsheet.mmCellPierceWidth
  expr: Constraints[29] = Spreadsheet.mmCellPierceWidth
  expr: Constraints[39] = Spreadsheet.mmCellPierceWidth
  expr: Constraints[49] = Spreadsheet.mmCellPierceWidth
  expr: Constraints[59] = Spreadsheet.mmCellPierceWidth
  expr: Constraints[69] = Spreadsheet.mmCellPierceWidth
  expr: Constraints[82] = Spreadsheet.mmCellWidth + Spreadsheet.mmCellWall
  expr: Constraints[83] = Spreadsheet.mmCellWidth + Spreadsheet.mmCellWall
  expr: Constraints[84] = Spreadsheet.mmCellWidth + Spreadsheet.mmCellWall
  expr: Constraints[85] = Spreadsheet.mmCellWidth + Spreadsheet.mmCellWall
  expr: Constraints[86] = Spreadsheet.mmCellWidth + Spreadsheet.mmCellWall
  expr: Constraints[87] = Spreadsheet.mmCellWidth + Spreadsheet.mmCellWall
  expr: Constraints[98] = Spreadsheet.mmCellPierceWidth
  expr: Constraints[9] = Spreadsheet.mmCellPierceWidth
  sketch-geometry (56):
    g0: ArcOfCircle CenterX=29 CenterY=0 CenterZ=0 NormalX=0 NormalY=0 NormalZ=1 AngleXU=0 Radius=3.0104 StartAngle=2.41495 EndAngle=3.86823
    g1: LineSegment StartX=26.75 StartY=2 StartZ=0 EndX=31.25 EndY=2 EndZ=0
    g2: LineSegment StartX=26.75 StartY=-2 StartZ=0 EndX=31.25 EndY=-2 EndZ=0
    g3: ArcOfCircle CenterX=29 CenterY=0 CenterZ=0 NormalX=0 NormalY=0 NormalZ=1 AngleXU=0 Radius=3.0104 StartAngle=5.55654 EndAngle=7.00983
    g4: ArcOfCircle CenterX=29 CenterY=9.8 CenterZ=0 NormalX=0 NormalY=0 NormalZ=1 AngleXU=0 Radius=3.0104 StartAngle=2.41495 EndAngle=3.86823
    g5: LineSegment StartX=26.75 StartY=11.8 StartZ=0 EndX=31.25 EndY=11.8 EndZ=0
    g6: LineSegment StartX=26.75 StartY=7.8 StartZ=0 EndX=31.25 EndY=7.8 EndZ=0
    g7: ArcOfCircle CenterX=29 CenterY=9.8 CenterZ=0 NormalX=0 NormalY=0 NormalZ=1 AngleXU=0 Radius=3.0104 StartAngle=5.55654 EndAngle=7.00983
    g8: ArcOfCircle CenterX=29 CenterY=19.6 CenterZ=0 NormalX=0 NormalY=0 NormalZ=1 AngleXU=0 Radius=3.0104 StartAngle=2.41495 EndAngle=3.86823
    g9: LineSegment StartX=26.75 StartY=21.6 StartZ=0 EndX=31.25 EndY=21.6 EndZ=0
    g10: LineSegment StartX=26.75 StartY=17.6 StartZ=0 EndX=31.25 EndY=17.6 EndZ=0
    g11: ArcOfCircle CenterX=29 CenterY=19.6 CenterZ=0 NormalX=0 NormalY=0 NormalZ=1 AngleXU=0 Radius=3.0104 StartAngle=5.55654 EndAngle=7.00983
    g12: ArcOfCircle CenterX=29 CenterY=29.4 CenterZ=0 NormalX=0 NormalY=0 NormalZ=1 AngleXU=0 Radius=3.0104 StartAngle=2.41495 EndAngle=3.86823
    g13: LineSegment StartX=26.75 StartY=31.4 StartZ=0 EndX=31.25 EndY=31.4 EndZ=0
    g14: LineSegment StartX=26.75 StartY=27.4 StartZ=0 EndX=31.25 EndY=27.4 EndZ=0
    g15: ArcOfCircle CenterX=29 CenterY=29.4 CenterZ=0 NormalX=0 NormalY=0 NormalZ=1 AngleXU=0 Radius=3.0104 StartAngle=5.55654 EndAngle=7.00983
    g16: ArcOfCircle CenterX=29 CenterY=-9.8 CenterZ=0 NormalX=0 NormalY=0 NormalZ=1 AngleXU=0 Radius=3.0104 StartAngle=2.41495 EndAngle=3.86823
    g17: LineSegment StartX=26.75 StartY=-7.8 StartZ=0 EndX=31.25 EndY=-7.8 EndZ=0
    g18: LineSegment StartX=26.75 StartY=-11.8 StartZ=0 EndX=31.25 EndY=-11.8 EndZ=0
    g19: ArcOfCircle CenterX=29 CenterY=-9.8 CenterZ=0 NormalX=0 NormalY=0 NormalZ=1 AngleXU=0 Radius=3.0104 StartAngle=5.55654 EndAngle=7.00983
    g20: ArcOfCircle CenterX=29 CenterY=-19.6 CenterZ=0 NormalX=0 NormalY=0 NormalZ=1 AngleXU=0 Radius=3.0104 StartAngle=2.41495 EndAngle=3.86823
    g21: LineSegment StartX=26.75 StartY=-17.6 StartZ=0 EndX=31.25 EndY=-17.6 EndZ=0
    g22: LineSegment StartX=26.75 StartY=-21.6 StartZ=0 EndX=31.25 EndY=-21.6 EndZ=0
    g23: ArcOfCircle CenterX=29 CenterY=-19.6 CenterZ=0 NormalX=0 NormalY=0 NormalZ=1 AngleXU=0 Radius=3.0104 StartAngle=5.55654 EndAngle=7.00983
    g24: ArcOfCircle CenterX=29 CenterY=-29.4 CenterZ=0 NormalX=0 NormalY=0 NormalZ=1 AngleXU=0 Radius=3.0104 StartAngle=2.41495 EndAngle=3.86823
    g25: LineSegment StartX=26.75 StartY=-27.4 StartZ=0 EndX=31.25 EndY=-27.4 EndZ=0
    g26: LineSegment StartX=26.75 StartY=-31.4 StartZ=0 EndX=31.25 EndY=-31.4 EndZ=0
    g27: ArcOfCircle CenterX=29 CenterY=-29.4 CenterZ=0 NormalX=0 NormalY=0 NormalZ=1 AngleXU=0 Radius=3.0104 StartAngle=5.55654 EndAngle=7.00983
    g28: ArcOfCircle CenterX=15 CenterY=0 CenterZ=0 NormalX=0 NormalY=0 NormalZ=1 AngleXU=0 Radius=3.0104 StartAngle=2.41495 EndAngle=3.86823
    g29: LineSegment StartX=12.75 StartY=2 StartZ=0 EndX=17.25 EndY=2 EndZ=0
    g30: LineSegment StartX=12.75 StartY=-2 StartZ=0 EndX=17.25 EndY=-2 EndZ=0
    g31: ArcOfCircle CenterX=15 CenterY=0 CenterZ=0 NormalX=0 NormalY=0 NormalZ=1 AngleXU=0 Radius=3.0104 StartAngle=5.55654 EndAngle=7.00983
    g32: ArcOfCircle CenterX=15 CenterY=9.8 CenterZ=0 NormalX=0 NormalY=0 NormalZ=1 AngleXU=0 Radius=3.0104 StartAngle=2.41495 EndAngle=3.86823
    g33: LineSegment StartX=12.75 StartY=11.8 StartZ=0 EndX=17.25 EndY=11.8 EndZ=0
    g34: LineSegment StartX=12.75 StartY=7.8 StartZ=0 EndX=17.25 EndY=7.8 EndZ=0
    g35: ArcOfCircle CenterX=15 CenterY=9.8 CenterZ=0 NormalX=0 NormalY=0 NormalZ=1 AngleXU=0 Radius=3.0104 StartAngle=5.55654 EndAngle=7.00983
    g36: ArcOfCircle CenterX=15 CenterY=19.6 CenterZ=0 NormalX=0 NormalY=0 NormalZ=1 AngleXU=0 Radius=3.0104 StartAngle=2.41495 EndAngle=3.86823
    g37: LineSegment StartX=12.75 StartY=21.6 StartZ=0 EndX=17.25 EndY=21.6 EndZ=0
    g38: LineSegment StartX=12.75 StartY=17.6 StartZ=0 EndX=17.25 EndY=17.6 EndZ=0
    g39: ArcOfCircle CenterX=15 CenterY=19.6 CenterZ=0 NormalX=0 NormalY=0 NormalZ=1 AngleXU=0 Radius=3.0104 StartAngle=5.55654 EndAngle=7.00983
    g40: ArcOfCircle CenterX=15 CenterY=29.4 CenterZ=0 NormalX=0 NormalY=0 NormalZ=1 AngleXU=0 Radius=3.0104 StartAngle=2.41495 EndAngle=3.86823
    g41: LineSegment StartX=12.75 StartY=31.4 StartZ=0 EndX=17.25 EndY=31.4 EndZ=0
    g42: LineSegment StartX=12.75 StartY=27.4 StartZ=0 EndX=17.25 EndY=27.4 EndZ=0
    g43: ArcOfCircle CenterX=15 CenterY=29.4 CenterZ=0 NormalX=0 NormalY=0 NormalZ=1 AngleXU=0 Radius=3.0104 StartAngle=5.55654 EndAngle=7.00983
    g44: ArcOfCircle CenterX=15 CenterY=-9.8 CenterZ=0 NormalX=0 NormalY=0 NormalZ=1 AngleXU=0 Radius=3.0104 StartAngle=2.41495 EndAngle=3.86823
    g45: LineSegment StartX=12.75 StartY=-7.8 StartZ=0 EndX=17.25 EndY=-7.8 EndZ=0
    g46: LineSegment StartX=12.75 StartY=-11.8 StartZ=0 EndX=17.25 EndY=-11.8 EndZ=0
    g47: ArcOfCircle CenterX=15 CenterY=-9.8 CenterZ=0 NormalX=0 NormalY=0 NormalZ=1 AngleXU=0 Radius=3.0104 StartAngle=5.55654 EndAngle=7.00983
    g48: ArcOfCircle CenterX=15 CenterY=-19.6 CenterZ=0 NormalX=0 NormalY=0 NormalZ=1 AngleXU=0 Radius=3.0104 StartAngle=2.41495 EndAngle=3.86823
    g49: LineSegment StartX=12.75 StartY=-17.6 StartZ=0 EndX=17.25 EndY=-17.6 EndZ=0
    g50: LineSegment StartX=12.75 StartY=-21.6 StartZ=0 EndX=17.25 EndY=-21.6 EndZ=0
    g51: ArcOfCircle CenterX=15 CenterY=-19.6 CenterZ=0 NormalX=0 NormalY=0 NormalZ=1 AngleXU=0 Radius=3.0104 StartAngle=5.55654 EndAngle=7.00983
    g52: ArcOfCircle CenterX=15 CenterY=-29.4 CenterZ=0 NormalX=0 NormalY=0 NormalZ=1 AngleXU=0 Radius=3.0104 StartAngle=2.41495 EndAngle=3.86823
    g53: LineSegment StartX=12.75 StartY=-27.4 StartZ=0 EndX=17.25 EndY=-27.4 EndZ=0
    g54: LineSegment StartX=12.75 StartY=-31.4 StartZ=0 EndX=17.25 EndY=-31.4 EndZ=0
    g55: ArcOfCircle CenterX=15 CenterY=-29.4 CenterZ=0 NormalX=0 NormalY=0 NormalZ=1 AngleXU=0 Radius=3.0104 StartAngle=5.55654 EndAngle=7.00983
  constraints (182):
    c: Horizontal(g1)
    c: Horizontal(g2)
    c: PointOnObject(g1,g0)
    c: Coincident(g0,g3)
    c: Coincident(g0,g2)
    c: Coincident(g3,g2)
    c: Coincident(g1,g0)
    c: Coincident(g3,g1)
    c: Equal(g2,g1)
    c: DistanceY(g2,g1) = 4
    c: Horizontal(g5)
    c: Horizontal(g6)
    c: PointOnObject(g5,g4)
    c: Coincident(g4,g7)
    c: Coincident(g4,g6)
    c: Coincident(g7,g6)
    c: Coincident(g5,g4)
    c: Coincident(g7,g5)
    c: Equal(g6,g5)
    c: DistanceY(g6,g5) = 4
    c: Horizontal(g9)
    c: Horizontal(g10)
    c: PointOnObject(g9,g8)
    c: Coincident(g8,g11)
    c: Coincident(g8,g10)
    c: Coincident(g11,g10)
    c: Coincident(g9,g8)
    c: Coincident(g11,g9)
    c: Equal(g10,g9)
    c: DistanceY(g10,g9) = 4
    c: Horizontal(g13)
    c: Horizontal(g14)
    c: PointOnObject(g13,g12)
    c: Coincident(g12,g15)
    c: Coincident(g12,g14)
    c: Coincident(g15,g14)
    c: Coincident(g13,g12)
    c: Coincident(g15,g13)
    c: Equal(g14,g13)
    c: DistanceY(g14,g13) = 4
    c: Horizontal(g17)
    c: Horizontal(g18)
    c: PointOnObject(g17,g16)
    c: Coincident(g16,g19)
    c: Coincident(g16,g18)
    c: Coincident(g19,g18)
    c: Coincident(g17,g16)
    c: Coincident(g19,g17)
    c: Equal(g18,g17)
    c: DistanceY(g18,g17) = 4
    c: Horizontal(g21)
    c: Horizontal(g22)
    c: PointOnObject(g21,g20)
    c: Coincident(g20,g23)
    c: Coincident(g20,g22)
    c: Coincident(g23,g22)
    c: Coincident(g21,g20)
    c: Coincident(g23,g21)
    c: Equal(g22,g21)
    c: DistanceY(g22,g21) = 4
    c: Horizontal(g25)
    c: Horizontal(g26)
    c: PointOnObject(g25,g24)
    c: Coincident(g24,g27)
    c: Coincident(g24,g26)
    c: Coincident(g27,g26)
    c: Coincident(g25,g24)
    c: Coincident(g27,g25)
    c: Equal(g26,g25)
    c: DistanceY(g26,g25) = 4
    c: Vertical(g0,g4)
    c: Vertical(g4,g8)
    c: Vertical(g8,g12)
    c: Vertical(g12,g16)
    c: Vertical(g16,g20)
    c: Vertical(g20,g24)
    c: Equal(g2,g18)
    c: Equal(g18,g22)
    c: Equal(g22,g26)
    c: Equal(g1,g5)
    c: Equal(g5,g9)
    c: Equal(g9,g13)
    c: DistanceY(g8,g12) = 9.8
    c: DistanceY(g4,g8) = 9.8
    c: DistanceY(g0,g4) = 9.8
    c: DistanceY(g16,g0) = 9.8
    c: DistanceY(g20,g16) = 9.8
    c: DistanceY(g24,g20) = 9.8
    c: PointOnObject(g0,g-1)
    c: Horizontal(g29)
    c: Horizontal(g30)
    c: PointOnObject(g29,g28)
    c: Coincident(g28,g31)
    c: Coincident(g28,g30)
    c: Coincident(g31,g30)
    c: Coincident(g29,g28)
    c: Coincident(g31,g29)
    c: Equal(g30,g29)
    c: DistanceY(g30,g29) = 4
    c: Horizontal(g33)
    c: Horizontal(g34)
    c: PointOnObject(g33,g32)
    c: Coincident(g32,g35)
    c: Coincident(g32,g34)
    c: Coincident(g35,g34)
    c: Coincident(g33,g32)
    c: Coincident(g35,g33)
    c: Equal(g34,g33)
    c: DistanceY(g34,g33) = 4
    c: Horizontal(g37)
    c: Horizontal(g38)
    c: PointOnObject(g37,g36)
    c: Coincident(g36,g39)
    c: Coincident(g36,g38)
    c: Coincident(g39,g38)
    c: Coincident(g37,g36)
    c: Coincident(g39,g37)
    c: Equal(g38,g37)
    c: DistanceY(g38,g37) = 4
    c: Horizontal(g41)
    c: Horizontal(g42)
    c: PointOnObject(g41,g40)
    c: Coincident(g40,g43)
    c: Coincident(g40,g42)
    c: Coincident(g43,g42)
    c: Coincident(g41,g40)
    c: Coincident(g43,g41)
    c: Equal(g42,g41)
    c: DistanceY(g42,g41) = 4
    c: Horizontal(g45)
    c: Horizontal(g46)
    c: PointOnObject(g45,g44)
    c: Coincident(g44,g47)
    c: Coincident(g44,g46)
    c: Coincident(g47,g46)
    c: Coincident(g45,g44)
    c: Coincident(g47,g45)
    c: Equal(g46,g45)
    c: DistanceY(g46,g45) = 4
    c: Horizontal(g49)
    c: Horizontal(g50)
    c: PointOnObject(g49,g48)
    c: Coincident(g48,g51)
    c: Coincident(g48,g50)
    c: Coincident(g51,g50)
    c: Coincident(g49,g48)
    c: Coincident(g51,g49)
    c: Equal(g50,g49)
    c: DistanceY(g50,g49) = 4
    c: Horizontal(g53)
    c: Horizontal(g54)
    c: PointOnObject(g53,g52)
    c: Coincident(g52,g55)
    c: Coincident(g52,g54)
    c: Coincident(g55,g54)
    c: Coincident(g53,g52)
    c: Coincident(g55,g53)
    c: Equal(g54,g53)
    c: DistanceY(g54,g53) = 4
    c: Vertical(g28,g32)
    c: Vertical(g32,g36)
    c: Vertical(g36,g40)
    c: Vertical(g40,g44)
    c: Vertical(g44,g48)
    c: Vertical(g48,g52)
    c: Equal(g30,g46)
    c: Equal(g46,g50)
    c: Equal(g50,g54)
    c: Equal(g29,g33)
    c: Equal(g33,g37)
    c: Equal(g37,g41)
    c: DistanceY(g36,g40) = 9.8
    c: DistanceY(g32,g36) = 9.8
    c: DistanceY(g28,g32) = 9.8
    c: DistanceY(g44,g28) = 9.8
    c: DistanceY(g48,g44) = 9.8
    c: DistanceY(g52,g48) = 9.8
    c: PointOnObject(g28,g-1)
    c: DistanceX(g24,g26) = 4.5
    c: DistanceX(g52,g54) = 4.5
    c: DistanceX(g-1,g28) = 15
    c: DistanceX(g28,g0) = 14
FEATURE [PartDesign::Pocket] Pocket  label="PiercesPocket"
  BaseFeature = -> Pad
  Direction = (-2e-16,2e-16,1)
  Length = 69.4
  Length2 = 5
  Midplane = true
  Profile = -> Sketch
  ReferenceAxis = -> Sketch [N_Axis]
  Type = 0
  expr: Length = Spreadsheet.mmBaseWidth + Spreadsheet.mmCellWall * 2
FEATURE [PartDesign::Body] Body004  label="BeamFixator"
  Group = -> [Sketch022,Pad,Sketch,Pocket]
  Origin = -> Origin005
  Tip = -> Pocket
COMPONENT P2 — recipe-attached ("HingePart", modeled in this document).
Construction recipe (the document's own serialized feature program — sketch geometry with constraints, then the solid features built on it; lengths are millimeters unless a unit is written):

FEATURE [PartDesign::LinearPattern] LinearPattern
  Direction = -> Sketch007 [V_Axis]
  Length = 67.8
  Occurrences = 4
  Originals = -> [Revolution,Revolution004,Pocket001,Pocket002,Pad008,Pad009,Pad010,Pad011,Pocket004,Pocket005]
  expr: Length = Spreadsheet.mmHingeHight
  expr: Occurrences = Spreadsheet.nHingeHightDiskCnt
FEATURE [PartDesign::Body] Body005
  Group = -> [LinearPattern]
  Origin = -> Origin007
  Tip = -> LinearPattern
COMPONENT P3 — recipe-attached ("AxisFixatorPart", modeled in this document).
Construction recipe (the document's own serialized feature program — sketch geometry with constraints, then the solid features built on it; lengths are millimeters unless a unit is written):

FEATURE [Sketcher::SketchObject] Sketch027  label="CommonFixatorScatch"
  FullyConstrained = false
  MapMode = 5
  Placement = pos=(0,0,0) rot=(0.57735,0.57735,0.57735;2.0944rad)
  Support = -> [YZ_Plane013]
  expr: Constraints[0] = Spreadsheet.mmAxisTubeDia + 2 * Spreadsheet.mmFixatorThick + 2 * Spreadsheet.mmTwoSideTapeThick
  expr: Constraints[17] = Spreadsheet.mmAxisTubeDia / 2 + Spreadsheet.mmPetalHightMax + Spreadsheet.mmTwoSideTapeThick
  expr: Constraints[18] = Spreadsheet.mmAxisTubeDia / 2 + Spreadsheet.mmPetalHightMax + Spreadsheet.mmTwoSideTapeThick
  expr: Constraints[32] = Spreadsheet.mmPetalPocketWidth
  expr: Constraints[33] = Spreadsheet.mmBaseWidth
  expr: Constraints[3] = Spreadsheet.mmAxisTubeDia
  sketch-geometry (14):
    g0: Circle CenterX=0 CenterY=0 CenterZ=0 NormalX=0 NormalY=0 NormalZ=1 AngleXU=0 Radius=26.72
    g1: LineSegment StartX=0 StartY=0 StartZ=0 EndX=32.2586 EndY=18.6245 EndZ=0
    g2: ArcOfCircle CenterX=0 CenterY=0 CenterZ=0 NormalX=0 NormalY=0 NormalZ=1 AngleXU=0 Radius=20.4 StartAngle=5.32461 EndAngle=6.86682
    g3: LineSegment StartX=0 StartY=-20.4 StartZ=0 EndX=0 EndY=-39.1443 EndZ=0
    g4: LineSegment StartX=0 StartY=-39.1443 StartZ=0 EndX=6.1902 EndY=-42.7183 EndZ=0
    g5: LineSegment StartX=6.1902 StartY=-42.7183 StartZ=0 EndX=40.0902 EndY=15.9983 EndZ=0
    g6: LineSegment StartX=40.0902 StartY=15.9983 StartZ=0 EndX=33.9 EndY=19.5722 EndZ=0
    g7: LineSegment StartX=33.9 StartY=19.5722 StartZ=0 EndX=17.6669 EndY=10.2 EndZ=0
    g8: LineSegment StartX=14.7156 StartY=-14.1284 StartZ=0 EndX=17.9224 EndY=-19.6828 EndZ=0
    g9: LineSegment StartX=17.9224 StartY=-19.6828 StartZ=0 EndX=8.08455 EndY=-25.3627 EndZ=0
    g10: LineSegment StartX=8.08455 StartY=-25.3627 StartZ=0 EndX=4.87772 EndY=-19.8083 EndZ=0
    g11: ArcOfCircle CenterX=0 CenterY=0 CenterZ=0 NormalX=0 NormalY=0 NormalZ=1 AngleXU=0 Radius=20.4 StartAngle=4.71239 EndAngle=4.95383
    g12: ArcOfCircle CenterX=0 CenterY=0 CenterZ=0 NormalX=0 NormalY=0 NormalZ=1 AngleXU=0 Radius=20.4 StartAngle=5.51814 EndAngle=6.80678
    g13: LineSegment StartX=0 StartY=0 StartZ=0 EndX=18.7992 EndY=-32.5612 EndZ=0
  constraints (39):
    c: Diameter(g0) = 53.44
    c: Angle(g-1,g1) = 0.523599
    c: PointOnObject(g6,g1)
    c: Diameter(g2) = 40.8
    c: Vertical(g3)
    c: Coincident(g3,g4)
    c: Coincident(g4,g5)
    c: Coincident(g5,g6)
    c: Coincident(g6,g7)
    c: Coincident(g8,g9)
    c: Coincident(g9,g10)
    c: Equal(g2,g11)
    c: Coincident(g2,g11)
    c: PointOnObject(g3,g-2)
    c: Parallel(g4,g6)
    c: Perpendicular(g5,g4)
    c: Tangent(g0,g5)
    c: Distance(g8,g11) = 26.62
    c: Distance(g9,g11) = 26.62
    c: Coincident(g11,g12)
    c: PointOnObject(g7,g1)
    c: Coincident(g10,g11)
    c: Coincident(g11,g3)
    c: Coincident(g12,g8)
    c: PointOnObject(g12,g1)
    c: Coincident(g12,g7)
    c: PointOnObject(g7,g1)
    c: Perpendicular(g10,g9)
    c: Perpendicular(g9,g8)
    c: Coincident(g13,g11)
    c: Angle(g13,g-1) = 1.0472
    c: Symmetric(g10,g8,g13)
    c: Distance(g10,g8) = 11.3598
    c: Distance(g4,g5) = 67.8
    c: Equal(g4,g6)
    c: Equal(g3,g7)
    c: Coincident(g-1,g0)
    c: Coincident(g0,g11)
    c: Coincident(g11,g1)
FEATURE [PartDesign::Pad] Pad012  label="AxisFixatorBodyPad"
  Direction = (1,-2e-16,3e-16)
  Length = 20.4
  Length2 = 10
  Placement = pos=(0,0,0) rot=(0.57735,0.57735,0.57735;2.0944rad)
  Profile = -> Sketch027
  ReferenceAxis = -> Sketch027 [N_Axis]
  Type = 0
  expr: Length = Spreadsheet.mmFixatorHight
FEATURE [Sketcher::SketchObject] Sketch031  label="MaxPetalBase001"
  FullyConstrained = false
  MapMode = 5
  Placement = pos=(0,0,0) rot=(0.57735,0.57735,0.57735;2.0944rad)
  Support = -> [YZ_Plane013]
  expr: Constraints[0] = Spreadsheet.mmAxisTubeDia + 2 * Spreadsheet.mmFixatorThick
  expr: Constraints[10] = Spreadsheet.mmAxisTubeDia
  expr: Constraints[12] = Spreadsheet.mmPetalPocketWidth
  expr: Constraints[1] = Spreadsheet.mmAxisTubeDia
  expr: Constraints[6] = Spreadsheet.mmAxisTubeDia / 2 + Spreadsheet.mmPetalHightMax
  sketch-geometry (7):
    g0: Circle CenterX=0 CenterY=2.5e-15 CenterZ=0 NormalX=0 NormalY=0 NormalZ=1 AngleXU=0 Radius=39.855
    g1: Circle CenterX=0 CenterY=2.5e-15 CenterZ=0 NormalX=0 NormalY=0 NormalZ=1 AngleXU=0 Radius=26.62
    g2: ArcOfCircle CenterX=0 CenterY=2.5e-15 CenterZ=0 NormalX=0 NormalY=0 NormalZ=1 AngleXU=0 Radius=20.4 StartAngle=5.86056 EndAngle=6.76902
    g3: LineSegment StartX=19.5933 StartY=5.67991 StartZ=0 EndX=26.52 EndY=5.67991 EndZ=0
    g4: LineSegment StartX=26.52 StartY=5.67991 StartZ=0 EndX=26.52 EndY=-5.67991 EndZ=0
    g5: LineSegment StartX=26.52 StartY=-5.67991 StartZ=0 EndX=19.5933 EndY=-5.67991 EndZ=0
    g6: ArcOfCircle CenterX=0 CenterY=2.5e-15 CenterZ=0 NormalX=0 NormalY=0 NormalZ=1 AngleXU=0 Radius=20.4 StartAngle=6.00103 EndAngle=6.56534
  constraints (17):
    c: Diameter(g1) = 53.24
    c: Diameter(g2) = 40.8
    c: Coincident(g3,g4)
    c: Coincident(g4,g5)
    c: Coincident(g0,g2)
    c: Vertical(g4)
    c: DistanceX(g-1,g4) = 26.52
    c: Coincident(g6,g0)
    c: Coincident(g6,g3)
    c: Coincident(g6,g5)
    c: Diameter(g6) = 40.8
    c: Symmetric(g3,g5,g-1)
    c: DistanceY(g5,g3) = 11.3598
    c: Horizontal(g3)
    c: Horizontal(g5)
    c: Coincident(g1,g6)
    c: Coincident(g-1,g6)
FEATURE [Sketcher::SketchObject] Sketch032  label="MinPetalBase001"
  AttachmentOffset = pos=(0,0,18.36) rot=(0,0,1;0rad)
  FullyConstrained = false
  MapMode = 5
  Placement = pos=(18.36,-4.1e-15,4.1e-15) rot=(0.57735,0.57735,0.57735;2.0944rad)
  Support = -> [YZ_Plane013]
  expr: .AttachmentOffset.Base.z = Spreadsheet.mmFixatorHight * 0.9
  expr: Constraints[0] = Spreadsheet.mmAxisTubeDia + 2 * Spreadsheet.mmFixatorThick
  expr: Constraints[10] = Spreadsheet.mmAxisTubeDia
  expr: Constraints[12] = Spreadsheet.mmPetalPocketWidth
  expr: Constraints[1] = Spreadsheet.mmAxisTubeDia
  expr: Constraints[6] = Spreadsheet.mmAxisTubeDia / 2 + Spreadsheet.mmPetalHightMin
  sketch-geometry (7):
    g0: Circle CenterX=0 CenterY=2e-15 CenterZ=0 NormalX=0 NormalY=0 NormalZ=1 AngleXU=0 Radius=39.844
    g1: Circle CenterX=0 CenterY=2e-15 CenterZ=0 NormalX=0 NormalY=0 NormalZ=1 AngleXU=0 Radius=26.62
    g2: ArcOfCircle CenterX=0 CenterY=2e-15 CenterZ=0 NormalX=0 NormalY=0 NormalZ=1 AngleXU=0 Radius=20.4 StartAngle=3.89517 EndAngle=6.7757
    g3: LineSegment StartX=19.5933 StartY=5.67991 StartZ=0 EndX=23.46 EndY=5.67991 EndZ=0
    g4: LineSegment StartX=23.46 StartY=5.67991 StartZ=0 EndX=23.46 EndY=-5.67991 EndZ=0
    g5: LineSegment StartX=23.46 StartY=-5.67991 StartZ=0 EndX=19.5933 EndY=-5.67991 EndZ=0
    g6: ArcOfCircle CenterX=0 CenterY=2e-15 CenterZ=0 NormalX=0 NormalY=0 NormalZ=1 AngleXU=0 Radius=20.4 StartAngle=6.00103 EndAngle=6.56534
  constraints (17):
    c: Diameter(g1) = 53.24
    c: Diameter(g2) = 40.8
    c: Coincident(g3,g4)
    c: Coincident(g4,g5)
    c: Coincident(g0,g2)
    c: Vertical(g4)
    c: DistanceX(g-1,g4) = 23.46
    c: Coincident(g6,g0)
    c: Coincident(g6,g3)
    c: Coincident(g6,g5)
    c: Diameter(g6) = 40.8
    c: Symmetric(g3,g5,g-1)
    c: DistanceY(g5,g3) = 11.3598
    c: Horizontal(g5)
    c: Horizontal(g3)
    c: Coincident(g1,g6)
    c: Coincident(g-1,g6)
FEATURE [PartDesign::SubtractiveLoft] SubtractiveLoft  label="PetalBodySubtractiveLoft"
  BaseFeature = -> Pad012
  Closed = false
  Placement = pos=(0,0,0) rot=(0.57735,0.57735,0.57735;2.0944rad)
  Profile = -> Sketch031
  Ruled = false
  Sections = -> [Sketch032]
FEATURE [PartDesign::PolarPattern] PolarPattern  label="ExisFixatorBodyPolarPattern"
  Angle = 360
  Axis = -> Sketch027 [N_Axis]
  BaseFeature = -> SubtractiveLoft
  Occurrences = 3
  Originals = -> [Pad012,AdditiveLoft,SubtractiveLoft]
  Placement = pos=(0,0,0) rot=(0.57735,0.57735,0.57735;2.0944rad)
FEATURE [PartDesign::Chamfer] Chamfer001
  Angle = 45
  Base = -> PolarPattern [Edge38,Edge9,Edge5,Edge23,Edge65,Edge59,Edge69,Edge47,Edge41]
  BaseFeature = -> PolarPattern
  ChamferType = 1
  FlipDirection = false
  Placement = pos=(0,0,0) rot=(0.57735,0.57735,0.57735;2.0944rad)
  Size = 2
  Size2 = 1
  SupportTransform = false
  UseAllEdges = false
FEATURE [PartDesign::Body] Body007  label="AxisFixatorBody"
  Group = -> [Sketch027,Pad012,Sketch031,Sketch032,SubtractiveLoft,PolarPattern,Chamfer001]
  Origin = -> Origin013
  Tip = -> Chamfer001
COMPONENT P4 — recipe-attached ("PetalMountingTemplate", modeled in this document).
Construction recipe (the document's own serialized feature program — sketch geometry with constraints, then the solid features built on it; lengths are millimeters unless a unit is written):

FEATURE [Sketcher::SketchObject] Sketch035  label="CommonFixatorScatch001"
  AttachmentOffset = pos=(0,0,16.32) rot=(0,0,1;0rad)
  FullyConstrained = false
  MapMode = 5
  Placement = pos=(16.32,-3.6e-15,3.6e-15) rot=(0.57735,0.57735,0.57735;2.0944rad)
  Support = -> [YZ_Plane013]
  expr: .AttachmentOffset.Base.z = Spreadsheet.mmFixatorHight * 0.8
  expr: Constraints[0] = Spreadsheet.mmAxisTubeDia + 2 * Spreadsheet.mmFixatorThick
  expr: Constraints[24] = Spreadsheet.mmBaseWidth
  expr: Constraints[3] = Spreadsheet.mmAxisTubeDia
  sketch-geometry (9):
    g0: Circle CenterX=0 CenterY=0 CenterZ=0 NormalX=0 NormalY=0 NormalZ=1 AngleXU=0 Radius=26.62
    g1: LineSegment StartX=0 StartY=0 StartZ=0 EndX=49.303 EndY=28.4651 EndZ=0
    g2: ArcOfCircle CenterX=0 CenterY=0 CenterZ=0 NormalX=0 NormalY=0 NormalZ=1 AngleXU=0 Radius=20.4 StartAngle=4.71235 EndAngle=6.7955
    g3: LineSegment StartX=0 StartY=-20.4 StartZ=0 EndX=0 EndY=-39.1443 EndZ=0
    g4: LineSegment StartX=0 StartY=-39.1443 StartZ=0 EndX=6.1036 EndY=-42.6683 EndZ=0
    g5: LineSegment StartX=6.1036 StartY=-42.6683 StartZ=0 EndX=40.0036 EndY=16.0483 EndZ=0
    g6: LineSegment StartX=40.0036 StartY=16.0483 StartZ=0 EndX=33.9 EndY=19.5722 EndZ=0
    g7: LineSegment StartX=33.9 StartY=19.5722 StartZ=0 EndX=17.6669 EndY=10.2 EndZ=0
    g8: ArcOfCircle CenterX=0 CenterY=0 CenterZ=0 NormalX=0 NormalY=0 NormalZ=1 AngleXU=0 Radius=20.4 StartAngle=4.71239 EndAngle=6.80678
  constraints (25):
    c: Diameter(g0) = 53.24
    c: Angle(g-1,g1) = 0.523599
    c: PointOnObject(g6,g1)
    c: Diameter(g2) = 40.8
    c: Vertical(g3)
    c: Coincident(g3,g4)
    c: Coincident(g4,g5)
    c: Coincident(g5,g6)
    c: Coincident(g6,g7)
    c: PointOnObject(g3,g-2)
    c: Parallel(g4,g6)
    c: Perpendicular(g5,g4)
    c: Tangent(g0,g5)
    c: PointOnObject(g8,g1)
    c: Coincident(g8,g7)
    c: PointOnObject(g8,g-2)
    c: PointOnObject(g8,g-1)
    c: PointOnObject(g8,g2)
    c: Coincident(g3,g8)
    c: Equal(g4,g6)
    c: Equal(g7,g3)
    c: Coincident(g2,g1)
    c: Coincident(g8,g1)
    c: Coincident(g8,g0)
    c: Distance(g4,g5) = 67.8
FEATURE [PartDesign::Pad] Pad013  label="AxisFixatorBodyPad001"
  Direction = (1,-2e-16,3e-16)
  Length = 6.12
  Length2 = 10
  Placement = pos=(0,0,0) rot=(0.57735,0.57735,0.57735;2.0944rad)
  Profile = -> Sketch035
  ReferenceAxis = -> Sketch035 [N_Axis]
  Type = 0
  expr: Length = Spreadsheet.mmFixatorHight * 0.3
FEATURE [Sketcher::SketchObject] Sketch038  label="MaxPetalBase004"
  FullyConstrained = false
  MapMode = 5
  Placement = pos=(0,0,0) rot=(0.57735,0.57735,0.57735;2.0944rad)
  Support = -> [YZ_Plane013]
  expr: Constraints[0] = Spreadsheet.mmAxisTubeDia + 2 * Spreadsheet.mmFixatorThick
  expr: Constraints[10] = Spreadsheet.mmAxisTubeDia
  expr: Constraints[15] = Spreadsheet.mmPetalPocketWidth
  expr: Constraints[1] = Spreadsheet.mmAxisTubeDia
  expr: Constraints[6] = Spreadsheet.mmAxisTubeDia * 2
  sketch-geometry (7):
    g0: Circle CenterX=0 CenterY=2.5e-15 CenterZ=0 NormalX=0 NormalY=0 NormalZ=1 AngleXU=0 Radius=39.855
    g1: Circle CenterX=0 CenterY=-1.1e-15 CenterZ=0 NormalX=0 NormalY=0 NormalZ=1 AngleXU=0 Radius=26.62
    g2: ArcOfCircle CenterX=0 CenterY=2.5e-15 CenterZ=0 NormalX=0 NormalY=0 NormalZ=1 AngleXU=0 Radius=20.4 StartAngle=5.6709 EndAngle=6.80795
    g3: LineSegment StartX=19.5933 StartY=5.67991 StartZ=0 EndX=81.6 EndY=5.67991 EndZ=0
    g4: LineSegment StartX=81.6 StartY=5.67991 StartZ=0 EndX=81.6 EndY=-5.67991 EndZ=0
    g5: LineSegment StartX=81.6 StartY=-5.67991 StartZ=0 EndX=19.5933 EndY=-5.67991 EndZ=0
    g6: ArcOfCircle CenterX=0 CenterY=2.5e-15 CenterZ=0 NormalX=0 NormalY=0 NormalZ=1 AngleXU=0 Radius=20.4 StartAngle=6.00103 EndAngle=6.56534
  constraints (16):
    c: Diameter(g1) = 53.24
    c: Diameter(g2) = 40.8
    c: Coincident(g3,g4)
    c: Coincident(g4,g5)
    c: Coincident(g0,g2)
    c: Vertical(g4)
    c: DistanceX(g-1,g4) = 81.6
    c: Coincident(g6,g0)
    c: Coincident(g6,g3)
    c: Coincident(g6,g5)
    c: Diameter(g6) = 40.8
    c: Horizontal(g3)
    c: Horizontal(g5)
    c: PointOnObject(g6,g-2)
    c: Symmetric(g3,g5,g-1)
    c: DistanceY(g5,g3) = 11.3598
FEATURE [Sketcher::SketchObject] Sketch039  label="MinPetalBase003"
  AttachmentOffset = pos=(0,0,20.4) rot=(0,0,1;0rad)
  FullyConstrained = false
  MapMode = 5
  Placement = pos=(20.4,-4.5e-15,4.5e-15) rot=(0.57735,0.57735,0.57735;2.0944rad)
  Support = -> [YZ_Plane013]
  expr: .AttachmentOffset.Base.z = Spreadsheet.mmFixatorHight
  expr: Constraints[0] = Spreadsheet.mmAxisTubeDia + 2 * Spreadsheet.mmFixatorThick
  expr: Constraints[10] = Spreadsheet.mmAxisTubeDia
  expr: Constraints[11] = Spreadsheet.mmPetalPocketWidth
  expr: Constraints[1] = Spreadsheet.mmAxisTubeDia
  expr: Constraints[6] = Spreadsheet.mmAxisTubeDia * 2
  sketch-geometry (7):
    g0: Circle CenterX=0 CenterY=2.1e-15 CenterZ=0 NormalX=0 NormalY=0 NormalZ=1 AngleXU=0 Radius=39.844
    g1: Circle CenterX=0 CenterY=2.1e-15 CenterZ=0 NormalX=0 NormalY=0 NormalZ=1 AngleXU=0 Radius=26.62
    g2: ArcOfCircle CenterX=0 CenterY=2.1e-15 CenterZ=0 NormalX=0 NormalY=0 NormalZ=1 AngleXU=0 Radius=20.4 StartAngle=3.90517 EndAngle=6.76925
    g3: LineSegment StartX=19.5933 StartY=5.67991 StartZ=0 EndX=81.6 EndY=5.67991 EndZ=0
    g4: LineSegment StartX=81.6 StartY=5.67991 StartZ=0 EndX=81.6 EndY=-5.67991 EndZ=0
    g5: LineSegment StartX=81.6 StartY=-5.67991 StartZ=0 EndX=19.5933 EndY=-5.67991 EndZ=0
    g6: ArcOfCircle CenterX=0 CenterY=2.1e-15 CenterZ=0 NormalX=0 NormalY=0 NormalZ=1 AngleXU=0 Radius=20.4 StartAngle=6.00103 EndAngle=6.56534
  constraints (17):
    c: Diameter(g1) = 53.24
    c: Diameter(g2) = 40.8
    c: Coincident(g3,g4)
    c: Coincident(g4,g5)
    c: Coincident(g0,g2)
    c: Vertical(g4)
    c: DistanceX(g-1,g4) = 81.6
    c: Coincident(g6,g0)
    c: Coincident(g6,g3)
    c: Coincident(g6,g5)
    c: Diameter(g6) = 40.8
    c: DistanceY(g5,g3) = 11.3598
    c: Symmetric(g3,g5,g-1)
    c: Coincident(g1,g6)
    c: Coincident(g-1,g6)
    c: Horizontal(g3)
    c: Horizontal(g5)
FEATURE [PartDesign::SubtractiveLoft] SubtractiveLoft001  label="PetalBodySubtractiveLoft001"
  BaseFeature = -> Pad013
  Closed = false
  Placement = pos=(0,0,0) rot=(0.57735,0.57735,0.57735;2.0944rad)
  Profile = -> Sketch038
  Ruled = false
  Sections = -> [Sketch039]
FEATURE [PartDesign::PolarPattern] PolarPattern001  label="ExisFixatorBodyPolarPattern001"
  Angle = 360
  Axis = -> Sketch035 [N_Axis]
  BaseFeature = -> SubtractiveLoft001
  Occurrences = 3
  Originals = -> [Pad013,SubtractiveLoft001]
  Placement = pos=(0,0,0) rot=(0.57735,0.57735,0.57735;2.0944rad)
FEATURE [Sketcher::SketchObject] Sketch040  label="CommonFixatorScatch002"
  AttachmentOffset = pos=(0,0,16.32) rot=(0,0,1;0rad)
  FullyConstrained = true
  MapMode = 5
  Placement = pos=(16.32,-3.6e-15,3.6e-15) rot=(0.57735,0.57735,0.57735;2.0944rad)
  Support = -> [YZ_Plane013]
  expr: .AttachmentOffset.Base.z = Spreadsheet.mmFixatorHight * 0.8
  expr: Constraints[11] = Spreadsheet.mmAxisTubeDia * 2
  expr: Constraints[14] = Spreadsheet.mmTemplatePartsConnectorDia - 2 * Spreadsheet.mmAirSpace
  expr: Constraints[15] = Spreadsheet.mmTemplatePartsConnectorDia * 3 / 2
  expr: Constraints[1] = Spreadsheet.mmAxisTubeDia + 2 * Spreadsheet.mmFixatorThick
  expr: Constraints[27] = Spreadsheet.mmAirSpace
  expr: Constraints[33] = Spreadsheet.mmTemplatePartsConnectorDia / 3
  expr: Constraints[41] = Spreadsheet.mmTemplatePartsConnectorDia
  expr: Constraints[43] = Spreadsheet.mmTemplatePartsConnectorDia * 2 / 3
  expr: Constraints[45] = Spreadsheet.mmTemplatePartsConnectorDia * 2 / 3 - 2 * Spreadsheet.mmAirSpace
  expr: Constraints[52] = Spreadsheet.mmTemplatePartsConnectorDia / 3
  expr: Constraints[55] = Spreadsheet.mmTemplatePartsConnectorDia / 2
  sketch-geometry (19):
    g0: Circle CenterX=0 CenterY=0 CenterZ=0 NormalX=0 NormalY=0 NormalZ=1 AngleXU=0 Radius=40.8
    g1: Circle CenterX=0 CenterY=0 CenterZ=0 NormalX=0 NormalY=0 NormalZ=1 AngleXU=0 Radius=26.62
    g2: LineSegment StartX=-35.5321 StartY=20.0526 StartZ=0 EndX=-28.3499 EndY=15.9059 EndZ=0
    g3: LineSegment StartX=22.767 StartY=-13.6064 StartZ=0 EndX=23.167 EndY=-12.9136 EndZ=0
    g4: LineSegment StartX=23.167 StartY=-12.9136 StartZ=0 EndX=21.4554 EndY=-11.9254 EndZ=0
    g5: LineSegment StartX=-35.1321 StartY=20.7454 StartZ=0 EndX=-35.5321 EndY=20.0526 EndZ=0
    g6: LineSegment StartX=23.0536 StartY=-13.31 StartZ=0 EndX=-35.3338 EndY=20.4 EndZ=0
    g7: ArcOfCircle CenterX=-26.42 CenterY=17.1754 CenterZ=0 NormalX=0 NormalY=0 NormalZ=1 AngleXU=0 Radius=2.31 StartAngle=4.65418 EndAngle=10.0066
    g8: LineSegment StartX=-26.5543 StartY=14.8693 StartZ=0 EndX=18.3629 EndY=-11.0637 EndZ=0
    g9: LineSegment StartX=-29.5129 StartY=17.5011 StartZ=0 EndX=-35.1321 EndY=20.7454 EndZ=0
    g10: LineSegment StartX=-35.1321 StartY=20.7454 StartZ=0 EndX=-35.5321 EndY=20.0526 EndZ=0
    g11: LineSegment StartX=-35.5321 StartY=20.0526 StartZ=0 EndX=22.851 EndY=-13.6549 EndZ=0
    g12: LineSegment StartX=22.851 StartY=-13.6549 StartZ=0 EndX=23.251 EndY=-12.9621 EndZ=0
    g13: LineSegment StartX=23.251 StartY=-12.9621 StartZ=0 EndX=-35.1321 EndY=20.7454 EndZ=0
    g14: ArcOfCircle CenterX=-26.42 CenterY=17.1754 CenterZ=0 NormalX=0 NormalY=0 NormalZ=1 AngleXU=0 Radius=3.11 StartAngle=5.34093 EndAngle=9.31984
    g15: ArcOfCircle CenterX=20.188 CenterY=-12.0474 CenterZ=0 NormalX=0 NormalY=0 NormalZ=1 AngleXU=0 Radius=2.07333 StartAngle=2.64723 EndAngle=5.73035
    g16: ArcOfCircle CenterX=20.188 CenterY=-12.0474 CenterZ=0 NormalX=0 NormalY=0 NormalZ=1 AngleXU=0 Radius=1.27333 StartAngle=1.99844 EndAngle=6.37914
    g17: LineSegment StartX=21.9524 StartY=-13.1361 StartZ=0 EndX=22.767 EndY=-13.6064 EndZ=0
    g18: LineSegment StartX=19.6599 StartY=-10.8888 StartZ=0 EndX=-24.5914 EndY=14.6597 EndZ=0
  constraints (56):
    c: PointOnObject(g6,g0)
    c: Diameter(g1) = 53.24
    c: Coincident(g0,g1)
    c: Coincident(g0,g-1)
    c: Coincident(g3,g4)
    c: Coincident(g9,g5)
    c: Coincident(g5,g2)
    c: Perpendicular(g3,g2)
    c: Symmetric(g2,g9,g6)
    c: Symmetric(g17,g3,g6)
    c: PointOnObject(g0,g6)
    c: Diameter(g0) = 81.6
    c: PointOnObject(g6,g1)
    c: Angle(g-1,g6) = 2.61799
    c: Diameter(g7) = 4.62
    c: Distance(g7,g5) = 9.33
    c: Parallel(g9,g4)
    c: Parallel(g2,g8)
    c: Coincident(g10,g11)
    c: Coincident(g11,g12)
    c: Coincident(g12,g13)
    c: Coincident(g13,g10)
    c: PointOnObject(g10,g0)
    c: Symmetric(g10,g10,g6)
    c: Parallel(g6,g13)
    c: Parallel(g11,g13)
    c: Coincident(g5,g10)
    c: Distance(g3,g3) = 0.8
    c: Coincident(g3,g17)
    c: PointOnObject(g11,g1)
    c: PointOnObject(g12,g1)
    c: PointOnObject(g3,g13)
    c: Distance(g6,g3) = 0.1
    c: Distance(g2,g8) = 2.07333
    c: PointOnObject(g14,g13)
    c: PointOnObject(g14,g13)
    c: PointOnObject(g18,g14)
    c: PointOnObject(g9,g14)
    c: Coincident(g7,g8)
    c: Coincident(g7,g2)
    c: Coincident(g14,g7)
    c: Diameter(g14) = 6.22
    c: PointOnObject(g18,g13)
    c: Diameter(g15) = 4.14667
    c: Coincident(g15,g16)
    c: Diameter(g16) = 2.54667
    c: Coincident(g15,g8)
    c: PointOnObject(g8,g11)
    c: Coincident(g17,g15)
    c: PointOnObject(g15,g11)
    c: Coincident(g4,g16)
    c: Coincident(g18,g16)
    c: Distance(g16,g4) = 2.07333
    c: PointOnObject(g4,g13)
    c: PointOnObject(g16,g13)
    c: Distance(g15,g12) = 3.11
FEATURE [PartDesign::Pocket] Pocket003
  BaseFeature = -> PolarPattern001
  Direction = (-1,2e-16,-3e-16)
  Length = 40.8
  Length2 = 5
  Midplane = true
  Placement = pos=(0,0,0) rot=(0.57735,0.57735,0.57735;2.0944rad)
  Profile = -> Sketch040
  ReferenceAxis = -> Sketch040 [N_Axis]
  Type = 0
  expr: Length = Spreadsheet.mmAxisTubeDia
FEATURE [PartDesign::Chamfer] Chamfer002
  Angle = 45
  Base = -> Pocket003 [Edge1,Edge35,Edge31,Edge98,Edge94,Edge47,Edge12]
  BaseFeature = -> Pocket003
  ChamferType = 0
  FlipDirection = false
  Placement = pos=(0,0,0) rot=(0.57735,0.57735,0.57735;2.0944rad)
  Size = 1
  Size2 = 1
  SupportTransform = false
  UseAllEdges = false
FEATURE [PartDesign::Chamfer] Chamfer003
  Angle = 45
  Base = -> Chamfer002 [Edge56,Edge17,Edge3,Edge28]
  BaseFeature = -> Chamfer002
  ChamferType = 0
  FlipDirection = false
  Placement = pos=(0,0,0) rot=(0.57735,0.57735,0.57735;2.0944rad)
  Size = 1
  Size2 = 1
  SupportTransform = false
  UseAllEdges = false
FEATURE [PartDesign::Chamfer] Chamfer004
  Angle = 45
  Base = -> Chamfer003 [Edge56,Edge61,Edge130,Edge128,Edge73,Edge75]
  BaseFeature = -> Chamfer003
  ChamferType = 0
  FlipDirection = false
  Placement = pos=(0,0,0) rot=(0.57735,0.57735,0.57735;2.0944rad)
  Size = 1
  Size2 = 1
  SupportTransform = false
  UseAllEdges = false
FEATURE [PartDesign::Fillet] Fillet
  Base = -> Chamfer004 [Edge66,Edge26]
  BaseFeature = -> Chamfer004
  Placement = pos=(0,0,0) rot=(0.57735,0.57735,0.57735;2.0944rad)
  Radius = 1
  SupportTransform = false
  UseAllEdges = false
FEATURE [PartDesign::Body] Body010  label="AxisFixatorTemplate"
  Group = -> [Sketch035,Pad013,Sketch038,Sketch039,SubtractiveLoft001,PolarPattern001,Sketch040,Pocket003,Chamfer002,Chamfer003,Chamfer004,Fillet]
  Origin = -> Origin019
  Tip = -> Fillet
COMPONENT P5 — recipe-attached ("AxisFixatorAbsolete", modeled in this document).
Construction recipe (the document's own serialized feature program — sketch geometry with constraints, then the solid features built on it; lengths are millimeters unless a unit is written):

FEATURE [Sketcher::SketchObject] Sketch041  label="CommonFixatorScatch003"
  FullyConstrained = false
  MapMode = 5
  Placement = pos=(0,0,0) rot=(0.57735,0.57735,0.57735;2.0944rad)
  Support = -> [YZ_Plane013]
  expr: Constraints[22] = 2 * (Spreadsheet.mmAxisTubeDia / 2 + Spreadsheet.mmFixatorThick) / cos(Spreadsheet.angPetal / 2)
  expr: Constraints[23] = Spreadsheet.mmHingeHight
  expr: Constraints[31] = Spreadsheet.mmAxisTubeDia
  expr: Constraints[64] = Spreadsheet.mmPetalWidth + Spreadsheet.mmAirSpace
  expr: Constraints[67] = Spreadsheet.mmAxisTubeDia / 2 + Spreadsheet.mmPetalHightMax + Spreadsheet.mmTwoSideTapeThick + Spreadsheet.mmAirSpace
  sketch-geometry (24):
    g0: LineSegment StartX=33.9 StartY=19.5722 StartZ=0 EndX=-33.9 EndY=19.5722 EndZ=0
    g1: LineSegment StartX=-33.9 StartY=19.5722 StartZ=0 EndX=0 EndY=-39.1443 EndZ=0
    g2: LineSegment StartX=0 StartY=-39.1443 StartZ=0 EndX=33.9 EndY=19.5722 EndZ=0
    g3: Circle CenterX=0 CenterY=0 CenterZ=0 NormalX=0 NormalY=0 NormalZ=1 AngleXU=0 Radius=39.1443
    g4: LineSegment StartX=-23.8668 StartY=13.7795 StartZ=0 EndX=-23.8668 EndY=-13.7795 EndZ=0
    g5: LineSegment StartX=-23.8668 StartY=-13.7795 StartZ=0 EndX=0 EndY=-27.5591 EndZ=0
    g6: LineSegment StartX=0 StartY=-27.5591 StartZ=0 EndX=23.8668 EndY=-13.7795 EndZ=0
    g7: LineSegment StartX=23.8668 StartY=-13.7795 StartZ=0 EndX=23.8668 EndY=13.7795 EndZ=0
    g8: LineSegment StartX=23.8668 StartY=13.7795 StartZ=0 EndX=0 EndY=27.5591 EndZ=0
    g9: LineSegment StartX=-1e-16 StartY=27.5591 StartZ=0 EndX=-23.8668 EndY=13.7795 EndZ=0
    g10: Circle CenterX=0 CenterY=0 CenterZ=0 NormalX=0 NormalY=0 NormalZ=1 AngleXU=0 Radius=27.5591
    g11: LineSegment StartX=0 StartY=0 StartZ=0 EndX=33.9 EndY=19.5722 EndZ=0
    g12: ArcOfCircle CenterX=0 CenterY=0 CenterZ=0 NormalX=0 NormalY=0 NormalZ=1 AngleXU=0 Radius=20.4 StartAngle=4.5996 EndAngle=6.79538
    g13: LineSegment StartX=0 StartY=-20.4 StartZ=0 EndX=0 EndY=-39.1443 EndZ=0
    g14: LineSegment StartX=0 StartY=-39.1443 StartZ=0 EndX=6.91684 EndY=-43.1378 EndZ=0
    g15: LineSegment StartX=6.91684 StartY=-43.1378 StartZ=0 EndX=40.8168 EndY=15.5787 EndZ=0
    g16: LineSegment StartX=40.8168 StartY=15.5787 StartZ=0 EndX=33.9 EndY=19.5722 EndZ=0
    g17: LineSegment StartX=33.9 StartY=19.5722 StartZ=0 EndX=17.6669 EndY=10.2 EndZ=0
    g18: LineSegment StartX=14.7156 StartY=-14.1284 StartZ=0 EndX=18.6289 EndY=-20.9065 EndZ=0
    g19: LineSegment StartX=18.6289 StartY=-20.9065 StartZ=0 EndX=8.79105 EndY=-26.5864 EndZ=0
    g20: LineSegment StartX=8.79105 StartY=-26.5864 StartZ=0 EndX=4.87772 EndY=-19.8083 EndZ=0
    g21: ArcOfCircle CenterX=0 CenterY=0 CenterZ=0 NormalX=0 NormalY=0 NormalZ=1 AngleXU=0 Radius=20.4 StartAngle=4.71239 EndAngle=4.95383
    g22: ArcOfCircle CenterX=0 CenterY=0 CenterZ=0 NormalX=0 NormalY=0 NormalZ=1 AngleXU=0 Radius=20.4 StartAngle=5.51814 EndAngle=6.80678
    g23: LineSegment StartX=0 StartY=0 StartZ=0 EndX=19.5722 EndY=-33.9 EndZ=0
  constraints (64):
    c: Coincident(g0,g1)
    c: Coincident(g1,g2)
    c: Coincident(g2,g0)
    c: Equal(g0,g1)
    c: Equal(g0,g2)
    c: PointOnObject(g0,g3)
    c: Coincident(g4,g5)
    c: Coincident(g5,g6)
    c: Coincident(g6,g7)
    c: Coincident(g7,g8)
    c: Coincident(g8,g9)
    c: Coincident(g9,g4)
    c: Equal(g4, g5-g9) x5
    c: PointOnObject(g4,g10)
    c: PointOnObject(g5,g10)
    c: PointOnObject(g6,g10)
    c: PointOnObject(g7,g10)
    c: PointOnObject(g8,g10)
    c: Diameter(g10) = 55.1181
    c: Distance(g2) = 67.8
    c: PointOnObject(g5,g-2)
    c: PointOnObject(g4,g10)
    c: Angle(g-1,g11) = 0.523599
    c: Coincident(g3,g10)
    c: Coincident(g3,g11)
    c: Coincident(g3,g-1)
    c: PointOnObject(g0,g11)
    c: Diameter(g12) = 40.8
    c: Coincident(g12,g3)
    c: Vertical(g13)
    c: Coincident(g13,g14)
    c: Coincident(g14,g15)
    c: Coincident(g15,g16)
    c: Coincident(g16,g17)
    c: Coincident(g19,g20)
    c: Coincident(g1,g13)
    c: Coincident(g0,g16)
    c: Equal(g12,g21)
    c: Coincident(g12,g21)
    c: PointOnObject(g13,g-2)
    c: PointOnObject(g13,g3)
    c: Parallel(g2,g15)
    c: Parallel(g14,g16)
    c: Perpendicular(g15,g14)
    c: Tangent(g10,g15)
    c: PointOnObject(g11,g3)
    c: Coincident(g21,g22)
    c: PointOnObject(g17,g11)
    c: Coincident(g20,g21)
    c: Coincident(g21,g13)
    c: Coincident(g22,g18)
    c: PointOnObject(g22,g11)
    c: Coincident(g22,g17)
    c: PointOnObject(g17,g11)
    c: Perpendicular(g20,g19)
    c: Perpendicular(g19,g18)
    c: Coincident(g23,g21)
    c: Angle(g23,g-2) = 2.61799
    c: PointOnObject(g23,g3)
    c: Symmetric(g20,g18,g23)
    c: Distance(g20,g18) = 11.3598
    c: Perpendicular(g23,g19)
    c: Coincident(g18,g19)
    c: Distance(g21,g19) = 27.42
FEATURE [PartDesign::Pad] Pad014  label="AxisFixatorBodyPad002"
  Direction = (1,-2e-16,3e-16)
  Length = 20.4
  Length2 = 10
  Placement = pos=(0,0,0) rot=(0.57735,0.57735,0.57735;2.0944rad)
  Profile = -> Sketch041
  ReferenceAxis = -> Sketch041 [N_Axis]
  Type = 0
  expr: Length = Spreadsheet.mmFixatorHight
FEATURE [Sketcher::SketchObject] Sketch044  label="MaxPetalBase006"
  FullyConstrained = false
  MapMode = 5
  Placement = pos=(0,0,0) rot=(0.57735,0.57735,0.57735;2.0944rad)
  Support = -> [YZ_Plane013]
  expr: Constraints[0] = Spreadsheet.mmAxisTubeDia + 2 * Spreadsheet.mmFixatorThick
  expr: Constraints[14] = Spreadsheet.mmPetalWidth + Spreadsheet.mmAirSpace
  expr: Constraints[1] = Spreadsheet.mmAxisTubeDia
  expr: Constraints[5] = Spreadsheet.mmAxisTubeDia / 2 + Spreadsheet.mmPetalHightMax
  expr: Constraints[9] = Spreadsheet.mmAxisTubeDia
  sketch-geometry (7):
    g0: Circle CenterX=0 CenterY=0 CenterZ=0 NormalX=0 NormalY=0 NormalZ=1 AngleXU=0 Radius=39.855
    g1: Circle CenterX=0 CenterY=0 CenterZ=0 NormalX=0 NormalY=0 NormalZ=1 AngleXU=0 Radius=26.62
    g2: ArcOfCircle CenterX=0 CenterY=0 CenterZ=0 NormalX=0 NormalY=0 NormalZ=1 AngleXU=0 Radius=20.4 StartAngle=5.86249 EndAngle=6.74499
    g3: LineSegment StartX=19.5933 StartY=5.67991 StartZ=0 EndX=26.52 EndY=5.67991 EndZ=0
    g4: LineSegment StartX=26.52 StartY=5.67991 StartZ=0 EndX=26.52 EndY=-5.67991 EndZ=0
    g5: LineSegment StartX=26.52 StartY=-5.67991 StartZ=0 EndX=19.5933 EndY=-5.67991 EndZ=0
    g6: ArcOfCircle CenterX=0 CenterY=0 CenterZ=0 NormalX=0 NormalY=0 NormalZ=1 AngleXU=0 Radius=20.4 StartAngle=6.00103 EndAngle=6.56534
  constraints (22):
    c: Diameter(g1) = 53.24
    c: Diameter(g2) = 40.8
    c: Coincident(g3,g4)
    c: Coincident(g4,g5)
    c: Coincident(g0,g2)
    c: DistanceX(g-1,g4) = 26.52
    c: Coincident(g6,g0)
    c: Coincident(g6,g3)
    c: Coincident(g6,g5)
    c: Diameter(g6) = 40.8
    c: Coincident(g6,g-1)
    c: Symmetric(g3,g5,g-1)
    c: Horizontal(g5)
    c: Horizontal(g3)
    c: DistanceY(g5,g3) = 11.3598
    c: Coincident(g6,g1)
    c: PointOnObject(g6,g-2)
    c: PointOnObject(g6,g-1)
    c: PointOnObject(g6,g5)
    c: PointOnObject(g6,g3)
    c: PointOnObject(g3,g6)
    c: Vertical(g4)
FEATURE [Sketcher::SketchObject] Sketch045  label="MinPetalBase005"
  AttachmentOffset = pos=(0,0,18.36) rot=(0,0,1;0rad)
  FullyConstrained = false
  MapMode = 5
  Placement = pos=(18.36,-4.1e-15,4.1e-15) rot=(0.57735,0.57735,0.57735;2.0944rad)
  Support = -> [YZ_Plane013]
  expr: .AttachmentOffset.Base.z = Spreadsheet.mmFixatorHight * 0.9
  expr: Constraints[0] = Spreadsheet.mmAxisTubeDia + 2 * Spreadsheet.mmFixatorThick
  expr: Constraints[10] = Spreadsheet.mmAxisTubeDia
  expr: Constraints[12] = Spreadsheet.mmPetalWidth + Spreadsheet.mmAirSpace
  expr: Constraints[1] = Spreadsheet.mmAxisTubeDia
  expr: Constraints[6] = Spreadsheet.mmAxisTubeDia / 2 + Spreadsheet.mmPetalHightMin
  sketch-geometry (7):
    g0: Circle CenterX=0 CenterY=2.3e-15 CenterZ=0 NormalX=0 NormalY=0 NormalZ=1 AngleXU=0 Radius=39.844
    g1: Circle CenterX=0 CenterY=2.3e-15 CenterZ=0 NormalX=0 NormalY=0 NormalZ=1 AngleXU=0 Radius=26.62
    g2: ArcOfCircle CenterX=0 CenterY=2.3e-15 CenterZ=0 NormalX=0 NormalY=0 NormalZ=1 AngleXU=0 Radius=20.4 StartAngle=3.8687 EndAngle=6.82101
    g3: LineSegment StartX=19.5933 StartY=5.67991 StartZ=0 EndX=23.46 EndY=5.67991 EndZ=0
    g4: LineSegment StartX=23.46 StartY=5.67991 StartZ=0 EndX=23.46 EndY=-5.67991 EndZ=0
    g5: LineSegment StartX=23.46 StartY=-5.67991 StartZ=0 EndX=19.5933 EndY=-5.67991 EndZ=0
    g6: ArcOfCircle CenterX=0 CenterY=2.3e-15 CenterZ=0 NormalX=0 NormalY=0 NormalZ=1 AngleXU=0 Radius=20.4 StartAngle=6.00103 EndAngle=6.56534
  constraints (17):
    c: Diameter(g1) = 53.24
    c: Diameter(g2) = 40.8
    c: Coincident(g3,g4)
    c: Coincident(g4,g5)
    c: Coincident(g0,g2)
    c: Vertical(g4)
    c: DistanceX(g-1,g4) = 23.46
    c: Coincident(g6,g0)
    c: Coincident(g6,g3)
    c: Coincident(g6,g5)
    c: Diameter(g6) = 40.8
    c: Symmetric(g3,g5,g-1)
    c: DistanceY(g5,g3) = 11.3598
    c: Horizontal(g3)
    c: Horizontal(g5)
    c: Coincident(g6,g1)
    c: Coincident(g6,g-1)
FEATURE [PartDesign::SubtractiveLoft] SubtractiveLoft002  label="PetalBodySubtractiveLoft002"
  BaseFeature = -> Pad014
  Closed = false
  Placement = pos=(0,0,0) rot=(0.57735,0.57735,0.57735;2.0944rad)
  Profile = -> Sketch044
  Ruled = false
  Sections = -> [Sketch045]
FEATURE [PartDesign::PolarPattern] PolarPattern002  label="ExisFixatorBodyPolarPattern002"
  Angle = 360
  Axis = -> Sketch041 [N_Axis]
  BaseFeature = -> SubtractiveLoft002
  Occurrences = 3
  Originals = -> [Pad014,SubtractiveLoft002]
  Placement = pos=(0,0,0) rot=(0.57735,0.57735,0.57735;2.0944rad)
FEATURE [PartDesign::Body] Body011  label="AxisFixatorBody001"
  Group = -> [Sketch041,Pad014,Sketch044,Sketch045,SubtractiveLoft002,PolarPattern002]
  Origin = -> Origin021
  Tip = -> PolarPattern002
COMPONENT P6 — recipe-attached ("PetalPart", modeled in this document).
Construction recipe (the document's own serialized feature program — sketch geometry with constraints, then the solid features built on it; lengths are millimeters unless a unit is written):

FEATURE [Sketcher::SketchObject] Sketch029  label="MaxPetalBase"
  FullyConstrained = false
  MapMode = 5
  Placement = pos=(0,0,0) rot=(0.57735,0.57735,0.57735;2.0944rad)
  Support = -> [YZ_Plane015]
  expr: Constraints[0] = Spreadsheet.mmAxisTubeDia + 2 * Spreadsheet.mmFixatorThick
  expr: Constraints[12] = Spreadsheet.mmAxisTubeDia / 2 + Spreadsheet.mmPetalHightMax
  expr: Constraints[16] = Spreadsheet.mmPetalWidth
  expr: Constraints[1] = Spreadsheet.mmAxisTubeDia
  expr: Constraints[6] = Spreadsheet.mmAxisTubeDia + Spreadsheet.mmTwoSideTapeThick * 2
  sketch-geometry (7):
    g0: Circle CenterX=0 CenterY=0 CenterZ=0 NormalX=0 NormalY=0 NormalZ=1 AngleXU=0 Radius=39.8652
    g1: Circle CenterX=0 CenterY=0 CenterZ=0 NormalX=0 NormalY=0 NormalZ=1 AngleXU=0 Radius=26.62
    g2: ArcOfCircle CenterX=0 CenterY=0 CenterZ=0 NormalX=0 NormalY=0 NormalZ=1 AngleXU=0 Radius=20.4 StartAngle=3.89684 EndAngle=6.80091
    g3: LineSegment StartX=19.8084 StartY=5.27991 StartZ=0 EndX=26.52 EndY=5.27991 EndZ=0
    g4: LineSegment StartX=26.52 StartY=5.27991 StartZ=0 EndX=26.52 EndY=-5.27991 EndZ=0
    g5: LineSegment StartX=26.52 StartY=-5.27991 StartZ=0 EndX=19.8084 EndY=-5.27991 EndZ=0
    g6: ArcOfCircle CenterX=0 CenterY=0 CenterZ=0 NormalX=0 NormalY=0 NormalZ=1 AngleXU=0 Radius=20.5 StartAngle=6.02269 EndAngle=6.54368
  constraints (20):
    c: Diameter(g1) = 53.24
    c: Diameter(g2) = 40.8
    c: Coincident(g3,g4)
    c: Coincident(g4,g5)
    c: PointOnObject(g3,g2)
    c: Coincident(g6,g0)
    c: Diameter(g6) = 41
    c: Coincident(g1,g6)
    c: Coincident(g0,g2)
    c: Vertical(g4)
    c: PointOnObject(g3,g6)
    c: PointOnObject(g5,g6)
    c: DistanceX(g-1,g4) = 26.52
    c: Horizontal(g3)
    c: Horizontal(g5)
    c: Symmetric(g5,g3,g-1)
    c: DistanceY(g5,g3) = 10.5598
    c: Coincident(g-1,g6)
    c: PointOnObject(g6,g5)
    c: PointOnObject(g6,g3)
FEATURE [Sketcher::SketchObject] Sketch030  label="MinPetalBase"
  AttachmentOffset = pos=(0,0,20.4) rot=(0,0,1;0rad)
  FullyConstrained = false
  MapMode = 5
  Placement = pos=(20.4,-4.5e-15,4.5e-15) rot=(0.57735,0.57735,0.57735;2.0944rad)
  Support = -> [YZ_Plane015]
  expr: .AttachmentOffset.Base.z = Spreadsheet.mmFixatorHight
  expr: Constraints[0] = Spreadsheet.mmAxisTubeDia + 2 * Spreadsheet.mmFixatorThick
  expr: Constraints[11] = Spreadsheet.mmAxisTubeDia / 2 + Spreadsheet.mmPetalHightMin
  expr: Constraints[15] = Spreadsheet.mmPetalWidth
  expr: Constraints[1] = Spreadsheet.mmAxisTubeDia
  expr: Constraints[5] = Spreadsheet.mmAxisTubeDia + Spreadsheet.mmTwoSideTapeThick * 2
  sketch-geometry (7):
    g0: Circle CenterX=0 CenterY=1.8e-15 CenterZ=0 NormalX=0 NormalY=0 NormalZ=1 AngleXU=0 Radius=39.865
    g1: Circle CenterX=0 CenterY=1.8e-15 CenterZ=0 NormalX=0 NormalY=0 NormalZ=1 AngleXU=0 Radius=26.62
    g2: ArcOfCircle CenterX=0 CenterY=1.8e-15 CenterZ=0 NormalX=0 NormalY=0 NormalZ=1 AngleXU=0 Radius=20.4 StartAngle=3.86544 EndAngle=6.7404
    g3: LineSegment StartX=19.8084 StartY=5.27991 StartZ=0 EndX=23.46 EndY=5.27991 EndZ=0
    g4: LineSegment StartX=23.46 StartY=5.27991 StartZ=0 EndX=23.46 EndY=-5.27991 EndZ=0
    g5: LineSegment StartX=23.46 StartY=-5.27991 StartZ=0 EndX=19.8084 EndY=-5.27991 EndZ=0
    g6: ArcOfCircle CenterX=0 CenterY=1.8e-15 CenterZ=0 NormalX=0 NormalY=0 NormalZ=1 AngleXU=0 Radius=20.5 StartAngle=6.02269 EndAngle=6.54368
  constraints (20):
    c: Diameter(g1) = 53.24
    c: Diameter(g2) = 40.8
    c: Coincident(g3,g4)
    c: Coincident(g4,g5)
    c: Coincident(g6,g0)
    c: Diameter(g6) = 41
    c: Coincident(g1,g6)
    c: Coincident(g0,g2)
    c: Vertical(g4)
    c: PointOnObject(g3,g6)
    c: PointOnObject(g5,g6)
    c: DistanceX(g-1,g4) = 23.46
    c: PointOnObject(g6,g5)
    c: PointOnObject(g6,g3)
    c: Coincident(g6,g-1)
    c: DistanceY(g5,g3) = 10.5598
    c: Symmetric(g5,g3,g-1)
    c: Horizontal(g3)
    c: Horizontal(g5)
    c: PointOnObject(g6,g-2)
FEATURE [PartDesign::AdditiveLoft] AdditiveLoft  label="PetalBodyBodyAdditiveLoft"
  Closed = false
  Placement = pos=(0,0,0) rot=(0.57735,0.57735,0.57735;2.0944rad)
  Profile = -> Sketch029
  Ruled = false
  Sections = -> [Sketch030]
FEATURE [PartDesign::Chamfer] Chamfer
  Angle = 45
  Base = -> AdditiveLoft [Edge8,Edge9,Edge6,Edge3,Edge2,Edge1,Edge11,Edge5]
  BaseFeature = -> AdditiveLoft
  ChamferType = 0
  FlipDirection = false
  Placement = pos=(0,0,0) rot=(0.57735,0.57735,0.57735;2.0944rad)
  Size = 1
  Size2 = 1
  SupportTransform = false
  UseAllEdges = false
FEATURE [PartDesign::Body] Body008  label="PetalBodyPart"
  Group = -> [Sketch029,Sketch030,AdditiveLoft,Chamfer]
  Origin = -> Origin015
  Tip = -> Chamfer
PROVENANCE & LICENSES
A FreeCAD (.FCStd) document from a public repository crawl; recipes are the document's own serialized feature recipes (and, for linked parts, companion documents' recipes).
License: as declared in the source repository (recorded in the dataset sidecar).
